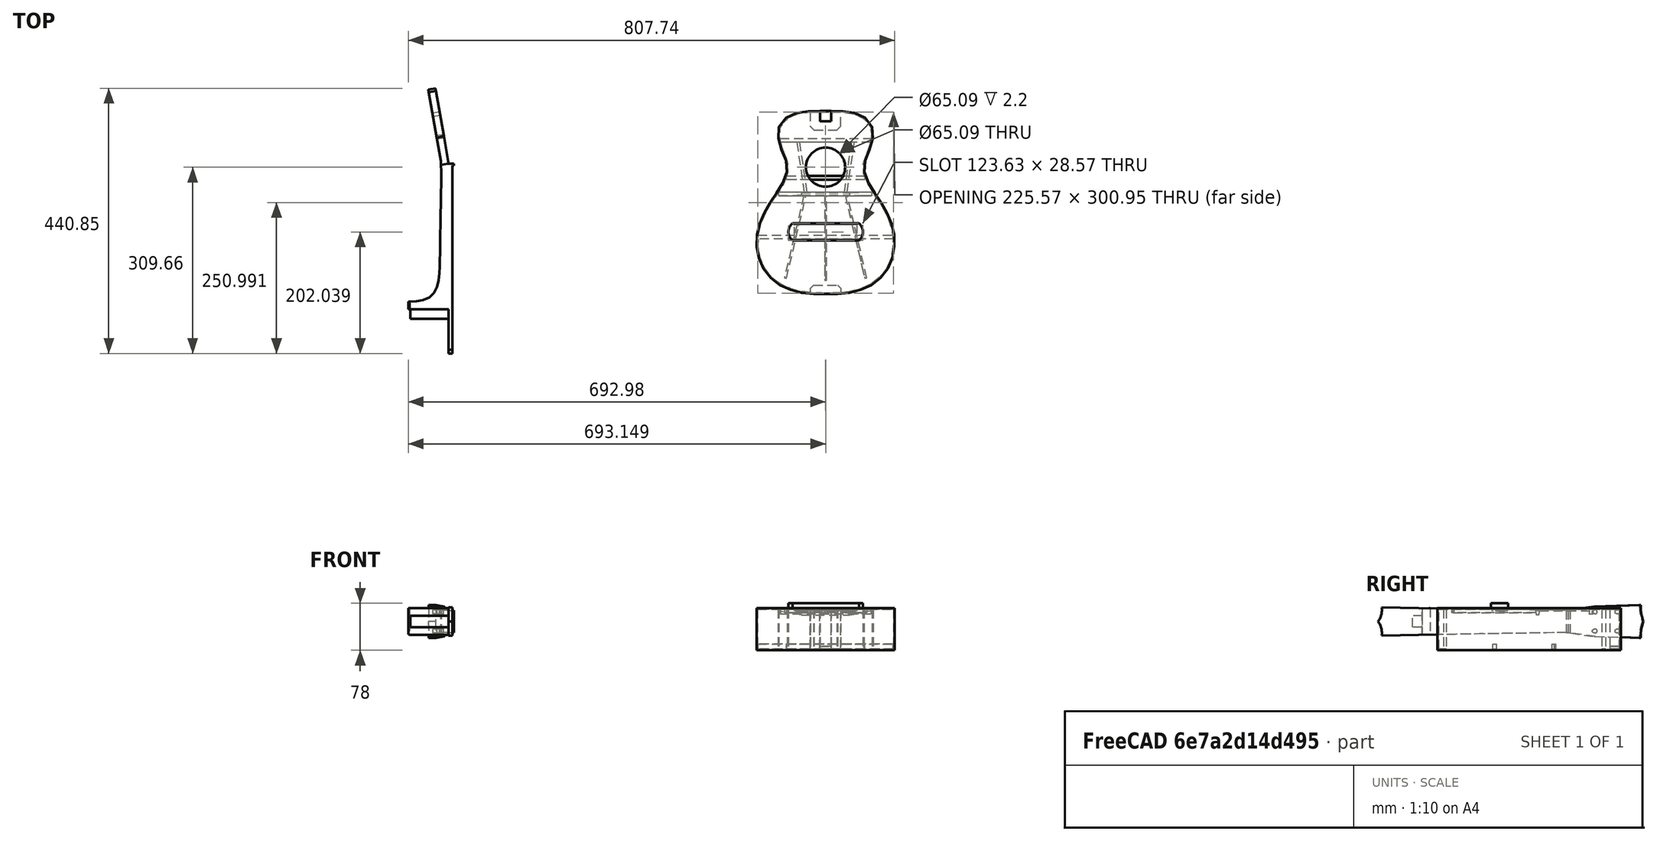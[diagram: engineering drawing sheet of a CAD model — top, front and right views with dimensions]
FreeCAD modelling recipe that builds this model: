
FCSTD DOCUMENT  (FreeCAD 1.0R39109 (Git))
Label: ukulele
License: All rights reserved
LicenseURL: http://en.wikipedia.org/wiki/All_rights_reserved
objects: Sketcher::SketchObject×50, PartDesign::Pad×34, TechDraw::DrawViewDimension×32, PartDesign::Pocket×12, Part::Part2DObjectPython×5, PartDesign::Body×5, TechDraw::DrawProjGroupItem×5, Part::Mirroring×4, App::FeaturePython×4, Spreadsheet::Sheet×3, TechDraw::DrawHatch×3, TechDraw::DrawSVGTemplate×2, App::Part×2, App::Link×2, TechDraw::DrawPage×2, TechDraw::DrawViewDimExtent×2, Image::ImagePlane×1, Part::Feature×1, App::DocumentObjectGroup×1, PartDesign::Hole×1, +3 more types
note: 313 computed .brp shape members not serialized (recipe doc carries the construction recipe); baked Part::Feature solids carry a one-line shape summary decoded from their .brp

FEATURE [Image::ImagePlane] uku
  Placement = pos=(-294.58,-157.27,0) rot=(0,0,1;0rad)
  XSize = 913.808
  YSize = 609.205
FEATURE [Sketcher::SketchObject] Sketch
  ArcFitTolerance = 1e-06
  AttachmentSupport = -> [XY_Plane]
  FullyConstrained = false
  MakeInternals = false
  MapMode = 5
  sketch-geometry (80):
    g0-g17: GeomPoint [constr] x18 (B-spline internal-alignment scaffolding for g18; pole/knot coordinates omitted)
    g18: BSplineCurve PolesCount=20 KnotsCount=18 Degree=3 IsPeriodic=0
    g19-g38: Circle [constr] x20 (B-spline internal-alignment scaffolding for g18; pole/knot coordinates omitted)
    g39: BSplineCurve PolesCount=20 KnotsCount=18 Degree=3 IsPeriodic=0
    g40-g57: GeomPoint [constr] x18 (B-spline internal-alignment scaffolding for g39; pole/knot coordinates omitted)
    g58-g77: Circle [constr] x20 (B-spline internal-alignment scaffolding for g39; pole/knot coordinates omitted)
    g78: LineSegment StartX=-9.55891 StartY=93.6205 StartZ=0 EndX=9.55891 EndY=93.6205 EndZ=0
    g79: LineSegment StartX=-0.843794 StartY=-211.013 StartZ=0 EndX=0.843794 EndY=-211.013 EndZ=0
  constraints (86):
    c: InternalAlignment(g0-g17 -> g18) x18
    c: InternalAlignment(g19,g18)
    c: Weight(g19) = 1
    c: InternalAlignment(g20,g18)
    c: Equal(g20,g19)
    c: InternalAlignment(g21,g18)
    c: Equal(g21,g19)
    c: InternalAlignment(g22,g18)
    c: Equal(g22,g19)
    c: InternalAlignment(g23,g18)
    c: Equal(g23,g19)
    c: InternalAlignment(g24,g18)
    c: Equal(g24,g19)
    c: InternalAlignment(g25,g18)
    c: Equal(g25,g19)
    c: InternalAlignment(g26,g18)
    c: Equal(g26,g19)
    c: InternalAlignment(g27,g18)
    c: Equal(g27,g19)
    c: InternalAlignment(g28,g18)
    c: Equal(g28,g19)
    c: InternalAlignment(g29,g18)
    c: Equal(g29,g19)
    c: InternalAlignment(g30,g18)
    c: Equal(g30,g19)
    c: InternalAlignment(g31,g18)
    c: Equal(g31,g19)
    c: InternalAlignment(g32,g18)
    c: Equal(g32,g19)
    c: InternalAlignment(g33,g18)
    c: Equal(g33,g19)
    c: InternalAlignment(g34,g18)
    c: Equal(g34,g19)
    c: InternalAlignment(g35,g18)
    c: Equal(g35,g19)
    c: InternalAlignment(g36,g18)
    c: Equal(g36,g19)
    c: InternalAlignment(g37,g18)
    c: Equal(g37,g19)
    c: InternalAlignment(g38,g18)
    c: Equal(g38,g19)
    c: InternalAlignment(g40-g77 -> g39) x38
    c: Equal(g19,g58)
    c: Symmetric(g19,g58,g-2)
    c: Equal(g20,g59)
    c: Symmetric(g20,g59,g-2)
    c: Equal(g21,g60)
    c: Symmetric(g21,g60,g-2)
    c: Equal(g22,g61)
    c: Symmetric(g22,g61,g-2)
    c: Equal(g23,g62)
    c: Symmetric(g23,g62,g-2)
    c: Equal(g24,g63)
    c: Symmetric(g24,g63,g-2)
    c: Equal(g25,g64)
    c: Symmetric(g25,g64,g-2)
    c: Equal(g26,g65)
    c: Symmetric(g26,g65,g-2)
    c: Equal(g27,g66)
    c: Symmetric(g27,g66,g-2)
    c: Equal(g28,g67)
    c: Symmetric(g28,g67,g-2)
    c: Equal(g29,g68)
    c: Symmetric(g29,g68,g-2)
    c: Equal(g30,g69)
    c: Symmetric(g30,g69,g-2)
    c: Equal(g31,g70)
    c: Symmetric(g31,g70,g-2)
    c: Equal(g32,g71)
    c: Symmetric(g32,g71,g-2)
    c: Equal(g33,g72)
    c: Symmetric(g33,g72,g-2)
    c: Equal(g34,g73)
    c: Symmetric(g34,g73,g-2)
    c: Equal(g35,g74)
    c: Symmetric(g35,g74,g-2)
    c: Equal(g36,g75)
    c: Symmetric(g36,g75,g-2)
    c: Equal(g37,g76)
    c: Symmetric(g37,g76,g-2)
    c: Equal(g38,g77)
    c: Symmetric(g38,g77,g-2)
    c: Coincident(g78,g18)
    c: Coincident(g78,g39)
    c: Coincident(g79,g18)
    c: Coincident(g79,g39)
FEATURE [Part::Feature] Sketch001
  shape: bbox 230.8 x 304.7 x 2e-07 mm, 0 faces, 0 solids (baked)
FEATURE [Part::Part2DObjectPython] BSpline  # Draft 2D object (typed FeaturePython)
  Area = 0
  Closed = false
  MakeFace = true
  Parameterization = 1
  Points = (23) [(-9.50482,86.1516,0),(-25.8136,85.9069,0),(-41.9527,84.3228,0),(-55.2551,79.961,0),(-66.5807,70.9788,0),(-71.3131,61.8385,0),(-70.9633,44.704,0),+16 more]
FEATURE [PartDesign::Body] Body  label="FIRST_TRY"
  AllowCompound = false
  Group = -> [Sketch,BSpline]
  Origin = -> Origin
FEATURE [Part::Part2DObjectPython] BSpline001  label="outerwall"  # Draft 2D object (typed FeaturePython)
  Area = 0
  Closed = false
  MakeFace = true
  Parameterization = 1
  Points = (31) [(-9.40108,93.5875,0),(-28.0476,93.1013,0),(-45.2362,91.0564,0),(-60.7631,84.8905,0),(-74.8327,72.6147,0),(-79.0928,58.2648,0),(-78.087,44.5074,0),+24 more]
FEATURE [Part::Part2DObjectPython] BSpline002  label="purfling"  # Draft 2D object (typed FeaturePython)
  Area = 0
  Closed = false
  MakeFace = true
  Parameterization = 1
  Points = (31) [(-9.32903,91.8043,0),(-27.9751,91.3181,0),(-44.8193,89.3211,0),(-59.8944,83.3315,0),(-73.3125,71.6798,0),(-77.3133,58.1294,0),(-76.3411,44.8772,0),+24 more]
FEATURE [Part::Part2DObjectPython] BSpline003  label="kerfing"  # Draft 2D object (typed FeaturePython)
  Area = 0
  Closed = false
  MakeFace = true
  Parameterization = 1
  Points = (31) [(-9.11273,86.4502,0),(-27.7574,85.9641,0),(-43.5674,84.1109,0),(-57.2858,78.6508,0),(-68.748,68.8728,0),(-71.9702,57.7226,0),(-71.0989,45.9877,0),+24 more]
FEATURE [Part::Mirroring] Mirror  label="outerwall (mirrored)"
  Base = (0,0,0)
  Normal = (1,0,0)
  Source = -> BSpline001
FEATURE [Part::Mirroring] Mirror001  label="kerfing (mirrored)"
  Base = (0,0,0)
  Normal = (1,0,0)
  Source = -> BSpline003
FEATURE [Part::Mirroring] Mirror002  label="purfling (mirrored)"
  Base = (0,0,0)
  Normal = (1,0,0)
  Source = -> BSpline002
FEATURE [Sketcher::SketchObject] Sketch002  label="base sketch"
  ArcFitTolerance = 1e-06
  FullyConstrained = false
  MakeInternals = false
  sketch-geometry (198):
    g0: BSplineCurve PolesCount=33 KnotsCount=31 Degree=3 IsPeriodic=0
    g1-g33: Circle [constr] x33 (B-spline internal-alignment scaffolding for g0; pole/knot coordinates omitted)
    g34-g64: GeomPoint [constr] x31 (B-spline internal-alignment scaffolding for g0; pole/knot coordinates omitted)
    g65: BSplineCurve PolesCount=33 KnotsCount=31 Degree=3 IsPeriodic=0
    g66-g98: Circle [constr] x33 (B-spline internal-alignment scaffolding for g65; pole/knot coordinates omitted)
    g99-g129: GeomPoint [constr] x31 (B-spline internal-alignment scaffolding for g65; pole/knot coordinates omitted)
    g130: BSplineCurve PolesCount=33 KnotsCount=31 Degree=3 IsPeriodic=0
    g131-g163: Circle [constr] x33 (B-spline internal-alignment scaffolding for g130; pole/knot coordinates omitted)
    g164-g194: GeomPoint [constr] x31 (B-spline internal-alignment scaffolding for g130; pole/knot coordinates omitted)
    g195: BSplineCurve PolesCount=33 KnotsCount=31 Degree=3 IsPeriodic=0
    g196: BSplineCurve PolesCount=33 KnotsCount=31 Degree=3 IsPeriodic=0
    g197: BSplineCurve PolesCount=33 KnotsCount=31 Degree=3 IsPeriodic=0
  constraints (201):
    c: InternalAlignment(g1,g0)
    c: Weight(g1) = 1
    c: InternalAlignment(g2,g0)
    c: Equal(g2,g1)
    c: InternalAlignment(g3,g0)
    c: Equal(g3,g1)
    c: InternalAlignment(g4,g0)
    c: Equal(g4,g1)
    c: InternalAlignment(g5,g0)
    c: Equal(g5,g1)
    c: InternalAlignment(g6,g0)
    c: Equal(g6,g1)
    c: InternalAlignment(g7,g0)
    c: Equal(g7,g1)
    c: InternalAlignment(g8,g0)
    c: Equal(g8,g1)
    c: InternalAlignment(g9,g0)
    c: Equal(g9,g1)
    c: InternalAlignment(g10,g0)
    c: Equal(g10,g1)
    c: InternalAlignment(g11,g0)
    c: Equal(g11,g1)
    c: InternalAlignment(g12,g0)
    c: Equal(g12,g1)
    c: InternalAlignment(g13,g0)
    c: Equal(g13,g1)
    c: InternalAlignment(g14,g0)
    c: Equal(g14,g1)
    c: InternalAlignment(g15,g0)
    c: Equal(g15,g1)
    c: InternalAlignment(g16,g0)
    c: Equal(g16,g1)
    c: InternalAlignment(g17,g0)
    c: Equal(g17,g1)
    c: InternalAlignment(g18,g0)
    c: Equal(g18,g1)
    c: InternalAlignment(g19,g0)
    c: Equal(g19,g1)
    c: InternalAlignment(g20,g0)
    c: Equal(g20,g1)
    c: InternalAlignment(g21,g0)
    c: Equal(g21,g1)
    c: InternalAlignment(g22,g0)
    c: Equal(g22,g1)
    c: InternalAlignment(g23,g0)
    c: Equal(g23,g1)
    c: InternalAlignment(g24,g0)
    c: Equal(g24,g1)
    c: InternalAlignment(g25,g0)
    c: Equal(g25,g1)
    c: InternalAlignment(g26,g0)
    c: Equal(g26,g1)
    c: InternalAlignment(g27,g0)
    c: Equal(g27,g1)
    c: InternalAlignment(g28,g0)
    c: Equal(g28,g1)
    c: InternalAlignment(g29,g0)
    c: Equal(g29,g1)
    c: InternalAlignment(g30,g0)
    c: Equal(g30,g1)
    c: InternalAlignment(g31,g0)
    c: Equal(g31,g1)
    c: InternalAlignment(g32,g0)
    c: Equal(g32,g1)
    c: InternalAlignment(g33,g0)
    c: Equal(g33,g1)
    c: InternalAlignment(g34-g64 -> g0) x31
    c: InternalAlignment(g66,g65)
    c: Weight(g66) = 1
    c: InternalAlignment(g67,g65)
    c: Equal(g67,g66)
    c: InternalAlignment(g68,g65)
    c: Equal(g68,g66)
    c: InternalAlignment(g69,g65)
    c: Equal(g69,g66)
    c: InternalAlignment(g70,g65)
    c: Equal(g70,g66)
    c: InternalAlignment(g71,g65)
    c: Equal(g71,g66)
    c: InternalAlignment(g72,g65)
    c: Equal(g72,g66)
    c: InternalAlignment(g73,g65)
    c: Equal(g73,g66)
    c: InternalAlignment(g74,g65)
    c: Equal(g74,g66)
    c: InternalAlignment(g75,g65)
    c: Equal(g75,g66)
    c: InternalAlignment(g76,g65)
    c: Equal(g76,g66)
    c: InternalAlignment(g77,g65)
    c: Equal(g77,g66)
    c: InternalAlignment(g78,g65)
    c: Equal(g78,g66)
    c: InternalAlignment(g79,g65)
    c: Equal(g79,g66)
    c: InternalAlignment(g80,g65)
    c: Equal(g80,g66)
    c: InternalAlignment(g81,g65)
    c: Equal(g81,g66)
    c: InternalAlignment(g82,g65)
    c: Equal(g82,g66)
    c: InternalAlignment(g83,g65)
    c: Equal(g83,g66)
    c: InternalAlignment(g84,g65)
    c: Equal(g84,g66)
    c: InternalAlignment(g85,g65)
    c: Equal(g85,g66)
    c: InternalAlignment(g86,g65)
    c: Equal(g86,g66)
    c: InternalAlignment(g87,g65)
    c: Equal(g87,g66)
    c: InternalAlignment(g88,g65)
    c: Equal(g88,g66)
    c: InternalAlignment(g89,g65)
    c: Equal(g89,g66)
    c: InternalAlignment(g90,g65)
    c: Equal(g90,g66)
    c: InternalAlignment(g91,g65)
    c: Equal(g91,g66)
    c: InternalAlignment(g92,g65)
    c: Equal(g92,g66)
    c: InternalAlignment(g93,g65)
    c: Equal(g93,g66)
    c: InternalAlignment(g94,g65)
    c: Equal(g94,g66)
    c: InternalAlignment(g95,g65)
    c: Equal(g95,g66)
    c: InternalAlignment(g96,g65)
    c: Equal(g96,g66)
    c: InternalAlignment(g97,g65)
    c: Equal(g97,g66)
    c: InternalAlignment(g98,g65)
    c: Equal(g98,g66)
    c: InternalAlignment(g99-g129 -> g65) x31
    c: InternalAlignment(g131,g130)
    c: Weight(g131) = 1
    c: InternalAlignment(g132,g130)
    c: Equal(g132,g131)
    c: InternalAlignment(g133,g130)
    c: Equal(g133,g131)
    c: InternalAlignment(g134,g130)
    c: Equal(g134,g131)
    c: InternalAlignment(g135,g130)
    c: Equal(g135,g131)
    c: InternalAlignment(g136,g130)
    c: Equal(g136,g131)
    c: InternalAlignment(g137,g130)
    c: Equal(g137,g131)
    c: InternalAlignment(g138,g130)
    c: Equal(g138,g131)
    c: InternalAlignment(g139,g130)
    c: Equal(g139,g131)
    c: InternalAlignment(g140,g130)
    c: Equal(g140,g131)
    c: InternalAlignment(g141,g130)
    c: Equal(g141,g131)
    c: InternalAlignment(g142,g130)
    c: Equal(g142,g131)
    c: InternalAlignment(g143,g130)
    c: Equal(g143,g131)
    c: InternalAlignment(g144,g130)
    c: Equal(g144,g131)
    c: InternalAlignment(g145,g130)
    c: Equal(g145,g131)
    c: InternalAlignment(g146,g130)
    c: Equal(g146,g131)
    c: InternalAlignment(g147,g130)
    c: Equal(g147,g131)
    c: InternalAlignment(g148,g130)
    c: Equal(g148,g131)
    c: InternalAlignment(g149,g130)
    c: Equal(g149,g131)
    c: InternalAlignment(g150,g130)
    c: Equal(g150,g131)
    c: InternalAlignment(g151,g130)
    c: Equal(g151,g131)
    c: InternalAlignment(g152,g130)
    c: Equal(g152,g131)
    c: InternalAlignment(g153,g130)
    c: Equal(g153,g131)
    c: InternalAlignment(g154,g130)
    c: Equal(g154,g131)
    c: InternalAlignment(g155,g130)
    c: Equal(g155,g131)
    c: InternalAlignment(g156,g130)
    c: Equal(g156,g131)
    c: InternalAlignment(g157,g130)
    c: Equal(g157,g131)
    c: InternalAlignment(g158,g130)
    c: Equal(g158,g131)
    c: InternalAlignment(g159,g130)
    c: Equal(g159,g131)
    c: InternalAlignment(g160,g130)
    c: Equal(g160,g131)
    c: InternalAlignment(g161,g130)
    c: Equal(g161,g131)
    c: InternalAlignment(g162,g130)
    c: Equal(g162,g131)
    c: InternalAlignment(g163,g130)
    c: Equal(g163,g131)
    c: InternalAlignment(g164-g194 -> g130) x31
FEATURE [Sketcher::SketchObject] Sketch003  label="vk"
  ArcFitTolerance = 1e-06
  FullyConstrained = false
  MakeInternals = false
  sketch-geometry (68):
    g0: BSplineCurve PolesCount=33 KnotsCount=31 Degree=3 IsPeriodic=0
    g1-g33: Circle [constr] x33 (B-spline internal-alignment scaffolding for g0; pole/knot coordinates omitted)
    g34-g64: GeomPoint [constr] x31 (B-spline internal-alignment scaffolding for g0; pole/knot coordinates omitted)
    g65: BSplineCurve PolesCount=33 KnotsCount=31 Degree=3 IsPeriodic=0
    g66: LineSegment StartX=-9.40108 StartY=93.5875 StartZ=0 EndX=9.40107 EndY=93.5875 EndZ=0
    g67: LineSegment StartX=-0.637124 StartY=-210.927 StartZ=0 EndX=0.637124 EndY=-210.927 EndZ=0
  constraints (73):
    c: InternalAlignment(g1,g0)
    c: Weight(g1) = 1
    c: InternalAlignment(g2,g0)
    c: Equal(g2,g1)
    c: InternalAlignment(g3,g0)
    c: Equal(g3,g1)
    c: InternalAlignment(g4,g0)
    c: Equal(g4,g1)
    c: InternalAlignment(g5,g0)
    c: Equal(g5,g1)
    c: InternalAlignment(g6,g0)
    c: Equal(g6,g1)
    c: InternalAlignment(g7,g0)
    c: Equal(g7,g1)
    c: InternalAlignment(g8,g0)
    c: Equal(g8,g1)
    c: InternalAlignment(g9,g0)
    c: Equal(g9,g1)
    c: InternalAlignment(g10,g0)
    c: Equal(g10,g1)
    c: InternalAlignment(g11,g0)
    c: Equal(g11,g1)
    c: InternalAlignment(g12,g0)
    c: Equal(g12,g1)
    c: InternalAlignment(g13,g0)
    c: Equal(g13,g1)
    c: InternalAlignment(g14,g0)
    c: Equal(g14,g1)
    c: InternalAlignment(g15,g0)
    c: Equal(g15,g1)
    c: InternalAlignment(g16,g0)
    c: Equal(g16,g1)
    c: InternalAlignment(g17,g0)
    c: Equal(g17,g1)
    c: InternalAlignment(g18,g0)
    c: Equal(g18,g1)
    c: InternalAlignment(g19,g0)
    c: Equal(g19,g1)
    c: InternalAlignment(g20,g0)
    c: Equal(g20,g1)
    c: InternalAlignment(g21,g0)
    c: Equal(g21,g1)
    c: InternalAlignment(g22,g0)
    c: Equal(g22,g1)
    c: InternalAlignment(g23,g0)
    c: Equal(g23,g1)
    c: InternalAlignment(g24,g0)
    c: Equal(g24,g1)
    c: InternalAlignment(g25,g0)
    c: Equal(g25,g1)
    c: InternalAlignment(g26,g0)
    c: Equal(g26,g1)
    c: InternalAlignment(g27,g0)
    c: Equal(g27,g1)
    c: InternalAlignment(g28,g0)
    c: Equal(g28,g1)
    c: InternalAlignment(g29,g0)
    c: Equal(g29,g1)
    c: InternalAlignment(g30,g0)
    c: Equal(g30,g1)
    c: InternalAlignment(g31,g0)
    c: Equal(g31,g1)
    c: InternalAlignment(g32,g0)
    c: Equal(g32,g1)
    c: InternalAlignment(g33,g0)
    c: Equal(g33,g1)
    c: InternalAlignment(g34-g64 -> g0) x31
    c: Coincident(g66,g0)
    c: Coincident(g66,g65)
    c: Horizontal(g66)
    c: Coincident(g67,g0)
    c: Coincident(g67,g65)
    c: Horizontal(g67)
FEATURE [PartDesign::Pad] Pad
  Direction = (0,0,1)
  Length = 2.2
  Length2 = 10
  Profile = -> Sketch003
  ReferenceAxis = -> Sketch003 [N_Axis]
  Reversed = true
  Suppressed = false
  Type = 0
  expr: Length = <<dimensies>>.DIKTE_FRONT
FEATURE [Spreadsheet::Sheet] Spreadsheet  label="dimensies"
  cells = A3='dikte front; B3(DIKTE_FRONT)=2.2; C3='mm; A4='diepte; B4(DIEPTE)=70
FEATURE [Sketcher::SketchObject] Sketch004
  ArcFitTolerance = 1e-06
  AttachmentSupport = -> [XY_Plane001]
  FullyConstrained = true
  MakeInternals = false
  MapMode = 5
  sketch-geometry (1):
    g0: Circle CenterX=0 CenterY=0 CenterZ=0 NormalX=0 NormalY=0 NormalZ=1 AngleXU=0 Radius=32.5435
  constraints (2):
    c: Coincident(g0,g-1)
    c: Diameter(g0) = 65.087
FEATURE [PartDesign::Pocket] Pocket
  BaseFeature = -> Pad
  Direction = (0,0,-1)
  Length = 5
  Length2 = 5
  Profile = -> Sketch004
  ReferenceAxis = -> Sketch004 [N_Axis]
  Suppressed = false
  Type = 2
FEATURE [Part::Part2DObjectPython] BSpline005  label="innerwall"  # Draft 2D object (typed FeaturePython)
  Area = 0
  Closed = false
  MakeFace = true
  Parameterization = 1
  Points = (31) [(-9.3204,91.5907,0),(-27.9664,91.1045,0),(-44.7693,89.1132,0),(-59.7903,83.1448,0),(-73.1303,71.5678,0),(-77.1001,58.1131,0),(-76.132,44.9215,0),+24 more]
FEATURE [Part::Mirroring] Mirror003  label="innerwall (mirrored)"
  Base = (0,-58.6691,0)
  Normal = (1,0,-1.19209e-07)
  Source = -> BSpline005
FEATURE [App::DocumentObjectGroup] Group  label="drafting"
  Group = -> [BSpline001,BSpline003,BSpline002,Mirror,Mirror002,Mirror001,BSpline005,Mirror003]
FEATURE [Sketcher::SketchObject] Sketch005  label="base sketch001"
  ArcFitTolerance = 1e-06
  FullyConstrained = false
  MakeInternals = false
  sketch-geometry (136):
    g0: BSplineCurve PolesCount=33 KnotsCount=31 Degree=3 IsPeriodic=0
    g1-g33: Circle [constr] x33 (B-spline internal-alignment scaffolding for g0; pole/knot coordinates omitted)
    g34-g64: GeomPoint [constr] x31 (B-spline internal-alignment scaffolding for g0; pole/knot coordinates omitted)
    g65: BSplineCurve PolesCount=33 KnotsCount=31 Degree=3 IsPeriodic=0
    g66-g98: Circle [constr] x33 (B-spline internal-alignment scaffolding for g65; pole/knot coordinates omitted)
    g99-g129: GeomPoint [constr] x31 (B-spline internal-alignment scaffolding for g65; pole/knot coordinates omitted)
    g130: BSplineCurve PolesCount=33 KnotsCount=31 Degree=3 IsPeriodic=0
    g131: BSplineCurve PolesCount=33 KnotsCount=31 Degree=3 IsPeriodic=0
    g132: LineSegment StartX=-9.32903 StartY=91.8043 StartZ=0 EndX=9.32903 EndY=91.8043 EndZ=0
    g133: LineSegment StartX=-9.40108 StartY=93.5875 StartZ=0 EndX=9.40107 EndY=93.5875 EndZ=0
    g134: LineSegment StartX=-0.629425 StartY=-209.143 StartZ=0 EndX=0.629425 EndY=-209.143 EndZ=0
    g135: LineSegment StartX=-0.637124 StartY=-210.927 StartZ=0 EndX=0.637124 EndY=-210.927 EndZ=0
  constraints (146):
    c: InternalAlignment(g1,g0)
    c: Weight(g1) = 1
    c: InternalAlignment(g2,g0)
    c: Equal(g2,g1)
    c: InternalAlignment(g3,g0)
    c: Equal(g3,g1)
    c: InternalAlignment(g4,g0)
    c: Equal(g4,g1)
    c: InternalAlignment(g5,g0)
    c: Equal(g5,g1)
    c: InternalAlignment(g6,g0)
    c: Equal(g6,g1)
    c: InternalAlignment(g7,g0)
    c: Equal(g7,g1)
    c: InternalAlignment(g8,g0)
    c: Equal(g8,g1)
    c: InternalAlignment(g9,g0)
    c: Equal(g9,g1)
    c: InternalAlignment(g10,g0)
    c: Equal(g10,g1)
    c: InternalAlignment(g11,g0)
    c: Equal(g11,g1)
    c: InternalAlignment(g12,g0)
    c: Equal(g12,g1)
    c: InternalAlignment(g13,g0)
    c: Equal(g13,g1)
    c: InternalAlignment(g14,g0)
    c: Equal(g14,g1)
    c: InternalAlignment(g15,g0)
    c: Equal(g15,g1)
    c: InternalAlignment(g16,g0)
    c: Equal(g16,g1)
    c: InternalAlignment(g17,g0)
    c: Equal(g17,g1)
    c: InternalAlignment(g18,g0)
    c: Equal(g18,g1)
    c: InternalAlignment(g19,g0)
    c: Equal(g19,g1)
    c: InternalAlignment(g20,g0)
    c: Equal(g20,g1)
    c: InternalAlignment(g21,g0)
    c: Equal(g21,g1)
    c: InternalAlignment(g22,g0)
    c: Equal(g22,g1)
    c: InternalAlignment(g23,g0)
    c: Equal(g23,g1)
    c: InternalAlignment(g24,g0)
    c: Equal(g24,g1)
    c: InternalAlignment(g25,g0)
    c: Equal(g25,g1)
    c: InternalAlignment(g26,g0)
    c: Equal(g26,g1)
    c: InternalAlignment(g27,g0)
    c: Equal(g27,g1)
    c: InternalAlignment(g28,g0)
    c: Equal(g28,g1)
    c: InternalAlignment(g29,g0)
    c: Equal(g29,g1)
    c: InternalAlignment(g30,g0)
    c: Equal(g30,g1)
    c: InternalAlignment(g31,g0)
    c: Equal(g31,g1)
    c: InternalAlignment(g32,g0)
    c: Equal(g32,g1)
    c: InternalAlignment(g33,g0)
    c: Equal(g33,g1)
    c: InternalAlignment(g34-g64 -> g0) x31
    c: InternalAlignment(g66,g65)
    c: Weight(g66) = 1
    c: InternalAlignment(g67,g65)
    c: Equal(g67,g66)
    c: InternalAlignment(g68,g65)
    c: Equal(g68,g66)
    c: InternalAlignment(g69,g65)
    c: Equal(g69,g66)
    c: InternalAlignment(g70,g65)
    c: Equal(g70,g66)
    c: InternalAlignment(g71,g65)
    c: Equal(g71,g66)
    c: InternalAlignment(g72,g65)
    c: Equal(g72,g66)
    c: InternalAlignment(g73,g65)
    c: Equal(g73,g66)
    c: InternalAlignment(g74,g65)
    c: Equal(g74,g66)
    c: InternalAlignment(g75,g65)
    c: Equal(g75,g66)
    c: InternalAlignment(g76,g65)
    c: Equal(g76,g66)
    c: InternalAlignment(g77,g65)
    c: Equal(g77,g66)
    c: InternalAlignment(g78,g65)
    c: Equal(g78,g66)
    c: InternalAlignment(g79,g65)
    c: Equal(g79,g66)
    c: InternalAlignment(g80,g65)
    c: Equal(g80,g66)
    c: InternalAlignment(g81,g65)
    c: Equal(g81,g66)
    c: InternalAlignment(g82,g65)
    c: Equal(g82,g66)
    c: InternalAlignment(g83,g65)
    c: Equal(g83,g66)
    c: InternalAlignment(g84,g65)
    c: Equal(g84,g66)
    c: InternalAlignment(g85,g65)
    c: Equal(g85,g66)
    c: InternalAlignment(g86,g65)
    c: Equal(g86,g66)
    c: InternalAlignment(g87,g65)
    c: Equal(g87,g66)
    c: InternalAlignment(g88,g65)
    c: Equal(g88,g66)
    c: InternalAlignment(g89,g65)
    c: Equal(g89,g66)
    c: InternalAlignment(g90,g65)
    c: Equal(g90,g66)
    c: InternalAlignment(g91,g65)
    c: Equal(g91,g66)
    c: InternalAlignment(g92,g65)
    c: Equal(g92,g66)
    c: InternalAlignment(g93,g65)
    c: Equal(g93,g66)
    c: InternalAlignment(g94,g65)
    c: Equal(g94,g66)
    c: InternalAlignment(g95,g65)
    c: Equal(g95,g66)
    c: InternalAlignment(g96,g65)
    c: Equal(g96,g66)
    c: InternalAlignment(g97,g65)
    c: Equal(g97,g66)
    c: InternalAlignment(g98,g65)
    c: Equal(g98,g66)
    c: InternalAlignment(g99-g129 -> g65) x31
    c: Coincident(g132,g65)
    c: Coincident(g132,g131)
    c: Horizontal(g132)
    c: Coincident(g133,g0)
    c: Coincident(g133,g130)
    c: Horizontal(g133)
    c: Coincident(g134,g65)
    c: Coincident(g134,g131)
    c: Horizontal(g134)
    c: Coincident(g135,g0)
    c: Coincident(g135,g130)
    c: Horizontal(g135)
FEATURE [PartDesign::Pad] Pad001
  BaseFeature = -> Pocket
  Direction = (0,0,1)
  Length = 70
  Length2 = 10
  Profile = -> Sketch005
  ReferenceAxis = -> Sketch005 [N_Axis]
  Refine = true
  Reversed = true
  Suppressed = false
  Type = 0
  expr: Length = 70
FEATURE [Sketcher::SketchObject] Sketch006
  ArcFitTolerance = 1e-06
  AttachmentSupport = -> [YZ_Plane001]
  ExternalGeometry = -> [Pad001]
  FullyConstrained = true
  MakeInternals = false
  MapMode = 5
  Placement = pos=(0,0,0) rot=(0.57735,0.57735,0.57735;2.0944rad)
  sketch-geometry (10):
    g0: GeomPoint X=0 Y=-2.2 Z=0
    g1: GeomPoint X=-44.45 Y=-2.2 Z=0
    g2: GeomPoint X=44.45 Y=-2.2 Z=0
    g3: LineSegment StartX=-47.625 StartY=-2.2 StartZ=0 EndX=-41.275 EndY=-2.2 EndZ=0
    g4: LineSegment StartX=-41.275 StartY=-2.2 StartZ=0 EndX=-41.275 EndY=-7.2 EndZ=0
    g5: LineSegment StartX=-41.275 StartY=-7.2 StartZ=0 EndX=-42.45 EndY=-11.725 EndZ=0
    g6: LineSegment StartX=-42.45 StartY=-11.725 StartZ=0 EndX=-46.45 EndY=-11.725 EndZ=0
    g7: LineSegment StartX=-46.45 StartY=-11.725 StartZ=0 EndX=-47.625 EndY=-7.2 EndZ=0
    g8: LineSegment StartX=-47.625 StartY=-7.2 StartZ=0 EndX=-47.625 EndY=-2.2 EndZ=0
    g9: GeomPoint X=-44.45 Y=-11.725 Z=0
  constraints (24):
    c: PointOnObject(g0,g-4)
    c: PointOnObject(g1,g-4)
    c: DistanceX(g1,g0) = 44.45
    c: Symmetric(g1,g2,g0)
    c: PointOnObject(g0,g-2)
    c: PointOnObject(g3,g-4)
    c: PointOnObject(g3,g-4)
    c: Coincident(g3,g4)
    c: Vertical(g4)
    c: Coincident(g4,g5)
    c: Coincident(g5,g6)
    c: Horizontal(g6)
    c: Coincident(g6,g7)
    c: Coincident(g7,g8)
    c: Coincident(g8,g3)
    c: Symmetric(g3,g3,g1)
    c: Vertical(g8)
    c: DistanceX(g3,g3) = 6.35
    c: Horizontal(g4,g7)
    c: DistanceY(g5,g3) = 9.525
    c: DistanceY(g8,g8) = 5
    c: Symmetric(g6,g6,g9)
    c: Vertical(g9,g1)
    c: DistanceX(g6,g9) = 2
FEATURE [PartDesign::Pad] Pad002
  BaseFeature = -> Pad001
  Direction = (1,0,0)
  Length = 155
  Length2 = 10
  Midplane = true
  Profile = -> Sketch006
  ReferenceAxis = -> Sketch006 [N_Axis]
  Refine = true
  Suppressed = false
  Type = 0
FEATURE [Sketcher::SketchObject] Sketch007
  ArcFitTolerance = 1e-06
  AttachmentSupport = -> [Pad002]
  ExternalGeometry = -> [Pad002]
  FullyConstrained = true
  MakeInternals = false
  MapMode = 5
  Placement = pos=(0,-41.275,0) rot=(0,0.707107,0.707107;3.14159rad)
  sketch-geometry (12):
    g0: GeomPoint X=40 Y=-11.725 Z=0
    g1: GeomPoint X=-40 Y=-11.725 Z=0
    g2: GeomPoint X=0 Y=-7.2 Z=0
    g3: GeomPoint X=-78.3882 Y=-4.2 Z=0
    g4: GeomPoint X=78.3882 Y=-4.2 Z=0
    g5: LineSegment StartX=78.3882 StartY=-4.2 StartZ=0 EndX=40 EndY=-11.725 EndZ=0
    g6: LineSegment StartX=-40 StartY=-11.725 StartZ=0 EndX=-78.3882 EndY=-4.2 EndZ=0
    g7: LineSegment StartX=40 StartY=-11.725 StartZ=0 EndX=-40 EndY=-11.725 EndZ=0
    g8: LineSegment StartX=78.3882 StartY=-4.2 StartZ=0 EndX=78.3882 EndY=-24.2 EndZ=0
    g9: LineSegment StartX=78.3882 StartY=-24.2 StartZ=0 EndX=-78.3882 EndY=-24.2 EndZ=0
    g10: LineSegment StartX=-78.3882 StartY=-4.2 StartZ=0 EndX=-78.3882 EndY=-24.2 EndZ=0
    g11: GeomPoint X=0 Y=-11.725 Z=0
  constraints (24):
    c: Symmetric(g-4,g-4,g2)
    c: PointOnObject(g3,g-6)
    c: PointOnObject(g4,g-5)
    c: Horizontal(g4,g3)
    c: DistanceX(g2,g0) = 40
    c: Coincident(g5,g4)
    c: Coincident(g5,g0)
    c: Coincident(g6,g1)
    c: DistanceY(g4,g-5) = 2
    c: Coincident(g7,g0)
    c: Coincident(g7,g1)
    c: Coincident(g8,g4)
    c: Vertical(g8)
    c: Coincident(g9,g8)
    c: Horizontal(g9)
    c: Coincident(g10,g9)
    c: Vertical(g10)
    c: DistanceY(g10,g10) = 20
    c: Coincident(g3,g10)
    c: Coincident(g3,g6)
    c: PointOnObject(g11,g-7)
    c: PointOnObject(g11,g-2)
    c: Symmetric(g1,g0,g11)
    c: Horizontal(g7)
FEATURE [PartDesign::Pocket] Pocket001
  BaseFeature = -> Pad002
  Direction = (0,-1,2e-16)
  Length = 9
  Length2 = 5
  Profile = -> Sketch007
  ReferenceAxis = -> Sketch007 [N_Axis]
  Refine = true
  Suppressed = false
  Type = 0
FEATURE [Sketcher::SketchObject] Sketch008
  ArcFitTolerance = 1e-06
  AttachmentSupport = -> [Pocket001]
  ExternalGeometry = -> [Pocket001]
  FullyConstrained = true
  MakeInternals = false
  MapMode = 5
  Placement = pos=(0,0,-2.2) rot=(1,0,0;3.14159rad)
  sketch-geometry (8):
    g0: LineSegment StartX=-25 StartY=209.143 StartZ=0 EndX=25 EndY=209.143 EndZ=0
    g1: GeomPoint X=-2.2048e-07 Y=209.143 Z=0
    g2: LineSegment StartX=-25 StartY=209.143 StartZ=0 EndX=-25 EndY=201.143 EndZ=0
    g3: LineSegment StartX=-25 StartY=201.143 StartZ=0 EndX=-20 EndY=196.143 EndZ=0
    g4: LineSegment StartX=-20 StartY=196.143 StartZ=0 EndX=20 EndY=196.143 EndZ=0
    g5: LineSegment StartX=20 StartY=196.143 StartZ=0 EndX=25 EndY=201.143 EndZ=0
    g6: LineSegment StartX=25 StartY=201.143 StartZ=0 EndX=25 EndY=209.143 EndZ=0
    g7: GeomPoint X=0 Y=196.143 Z=0
  constraints (19):
    c: Horizontal(g0)
    c: Symmetric(g0,g0,g1)
    c: Symmetric(g-4,g-3,g1)
    c: DistanceX(g0,g0) = 50
    c: Coincident(g0,g2)
    c: Vertical(g2)
    c: Coincident(g2,g3)
    c: Coincident(g3,g4)
    c: Horizontal(g4)
    c: Coincident(g4,g5)
    c: Coincident(g5,g6)
    c: Coincident(g6,g0)
    c: Vertical(g6)
    c: Symmetric(g4,g4,g7)
    c: PointOnObject(g7,g-2)
    c: Angle(g3,g2) = 2.35619
    c: DistanceY(g6,g6) = 8
    c: DistanceX(g4,g4) = 40
    c: Horizontal(g2,g5)
FEATURE [PartDesign::Pad] Pad003
  BaseFeature = -> Pocket001
  Direction = (0,0,-1)
  Length = 65.6
  Length2 = 10
  Profile = -> Sketch008
  ReferenceAxis = -> Sketch008 [N_Axis]
  Refine = true
  Suppressed = false
  Type = 0
  expr: Length = <<dimensies>>.DIEPTE - 2 * <<dimensies>>.DIKTE_FRONT
FEATURE [Sketcher::SketchObject] Sketch009
  ArcFitTolerance = 1e-06
  AttachmentSupport = -> [Pad003]
  FullyConstrained = true
  MakeInternals = false
  MapMode = 5
  Placement = pos=(0,0,-2.2) rot=(1,0,0;3.14159rad)
  sketch-geometry (12):
    g0: LineSegment StartX=-25.4 StartY=-92.925 StartZ=0 EndX=-25.4 EndY=-68.289 EndZ=0
    g1: LineSegment StartX=-25.4 StartY=-68.289 StartZ=0 EndX=-19.036 EndY=-61.925 EndZ=0
    g2: LineSegment StartX=-19.036 StartY=-61.925 StartZ=0 EndX=19.036 EndY=-61.925 EndZ=0
    g3: LineSegment StartX=19.036 StartY=-61.925 StartZ=0 EndX=25.4 EndY=-68.289 EndZ=0
    g4: LineSegment StartX=25.4 StartY=-68.289 StartZ=0 EndX=25.4 EndY=-92.925 EndZ=0
    g5: LineSegment StartX=25.4 StartY=-92.925 StartZ=0 EndX=9.525 EndY=-92.925 EndZ=0
    g6: LineSegment StartX=9.525 StartY=-92.925 StartZ=0 EndX=9.525 EndY=-75.525 EndZ=0
    g7: LineSegment StartX=9.525 StartY=-75.525 StartZ=0 EndX=-9.525 EndY=-75.525 EndZ=0
    g8: LineSegment StartX=-9.525 StartY=-75.525 StartZ=0 EndX=-9.525 EndY=-92.925 EndZ=0
    g9: LineSegment StartX=-9.525 StartY=-92.925 StartZ=0 EndX=-25.4 EndY=-92.925 EndZ=0
    g10: GeomPoint X=0 Y=-61.925 Z=0
    g11: GeomPoint X=0 Y=-75.525 Z=0
  constraints (32):
    c: Vertical(g0)
    c: Coincident(g0,g1)
    c: Coincident(g1,g2)
    c: Horizontal(g2)
    c: Coincident(g2,g3)
    c: Coincident(g3,g4)
    c: Vertical(g4)
    c: Coincident(g4,g5)
    c: Horizontal(g5)
    c: Coincident(g5,g6)
    c: Vertical(g6)
    c: Coincident(g6,g7)
    c: Horizontal(g7)
    c: Coincident(g7,g8)
    c: Vertical(g8)
    c: Coincident(g8,g9)
    c: Coincident(g9,g0)
    c: Horizontal(g9)
    c: Symmetric(g2,g2,g10)
    c: Symmetric(g7,g7,g11)
    c: PointOnObject(g11,g-2)
    c: PointOnObject(g10,g-2)
    c: Angle(g0,g1) = 2.35619
    c: Horizontal(g3,g0)
    c: Equal(g9,g5)
    c: DistanceX(g8,g5) = 19.05
    c: DistanceY(g0,g1) = 31
    c: DistanceY(g8,g8) = 17.4
    c: Horizontal(g8,g5)
    c: DistanceX(g0,g4) = 50.8
    c: Distance(g1,g1) = 9
    c: Block(g2)
FEATURE [PartDesign::Pad] Pad004
  BaseFeature = -> Pad003
  Direction = (0,0,-1)
  Length = 65.6
  Length2 = 10
  Profile = -> Sketch009
  ReferenceAxis = -> Sketch009 [N_Axis]
  Refine = true
  Suppressed = false
  Type = 0
  expr: Length = <<dimensies>>.DIEPTE - 2 * <<dimensies>>.DIKTE_FRONT
FEATURE [Sketcher::SketchObject] Sketch010
  ArcFitTolerance = 1e-06
  AttachmentSupport = -> [Pad004]
  ExternalGeometry = -> [Pad004,Sketch003]
  FullyConstrained = true
  MakeInternals = false
  MapMode = 5
  Placement = pos=(0,93.5875,0) rot=(0,0.707107,0.707107;3.14159rad)
  sketch-geometry (4):
    g0: LineSegment StartX=-9.40107 StartY=0 StartZ=0 EndX=-9.40107 EndY=-63.5 EndZ=0
    g1: LineSegment StartX=-9.40107 StartY=-63.5 StartZ=0 EndX=9.40108 EndY=-63.5 EndZ=0
    g2: LineSegment StartX=9.40108 StartY=-63.5 StartZ=0 EndX=9.40108 EndY=0 EndZ=0
    g3: LineSegment StartX=9.40108 StartY=0 StartZ=0 EndX=-9.40107 EndY=0 EndZ=0
  constraints (10):
    c: Coincident(g0,g1)
    c: Coincident(g1,g2)
    c: Coincident(g2,g3)
    c: Coincident(g3,g0)
    c: Vertical(g0)
    c: Vertical(g2)
    c: Horizontal(g1)
    c: Coincident(g0,g-6)
    c: Coincident(g-6,g2)
    c: DistanceY(g0,g0) = 63.5
FEATURE [PartDesign::Pocket] Pocket002
  BaseFeature = -> Pad004
  Direction = (0,-1,2e-16)
  Length = 17.5
  Length2 = 5
  Profile = -> Sketch010
  ReferenceAxis = -> Sketch010 [N_Axis]
  Refine = true
  Suppressed = false
  Type = 0
FEATURE [Sketcher::SketchObject] Sketch011
  ArcFitTolerance = 1e-06
  AttachmentSupport = -> [Pocket002]
  FullyConstrained = false
  MakeInternals = false
  MapMode = 5
  Placement = pos=(0,0,-2.2) rot=(1,0,0;3.14159rad)
  sketch-geometry (6):
    g0: LineSegment StartX=-52 StartY=120.048 StartZ=0 EndX=-52 EndY=95.0481 EndZ=0
    g1: LineSegment StartX=-52 StartY=95.0481 StartZ=0 EndX=52 EndY=95.0481 EndZ=0
    g2: LineSegment StartX=52 StartY=95.0481 StartZ=0 EndX=52 EndY=120.048 EndZ=0
    g3: LineSegment StartX=52 StartY=120.048 StartZ=0 EndX=-52 EndY=120.048 EndZ=0
    g4: GeomPoint X=1e-16 Y=120.048 Z=0
    g5: GeomPoint X=0 Y=105.469 Z=0
  constraints (13):
    c: Coincident(g0,g1)
    c: Coincident(g1,g2)
    c: Coincident(g2,g3)
    c: Coincident(g3,g0)
    c: Vertical(g0)
    c: Vertical(g2)
    c: Horizontal(g3)
    c: PointOnObject(g5,g-2)
    c: Symmetric(g0,g2,g4)
    c: Symmetric(g1,g0,g-2)
    c: DistanceY(g0,g0) = 25
    c: DistanceX(g3,g3) = 104
    c: Block(g3)
FEATURE [PartDesign::Pad] Pad005
  BaseFeature = -> Pocket002
  Direction = (0,0,-1)
  Length = 2.2
  Length2 = 10
  Profile = -> Sketch011
  ReferenceAxis = -> Sketch011 [N_Axis]
  Refine = true
  Suppressed = false
  Type = 0
  expr: Length = <<dimensies>>.DIKTE_FRONT
FEATURE [Sketcher::SketchObject] Sketch012
  ArcFitTolerance = 1e-06
  AttachmentSupport = -> [Pad005]
  FullyConstrained = true
  MakeInternals = false
  MapMode = 5
  sketch-geometry (5):
    g0: LineSegment StartX=-54.9901 StartY=-93.3363 StartZ=0 EndX=55.5099 EndY=-93.3363 EndZ=0
    g1: LineSegment StartX=-54.9901 StartY=-121.906 StartZ=0 EndX=55.5099 EndY=-121.906 EndZ=0
    g2: ArcOfCircle CenterX=-42.9824 CenterY=-107.621 CenterZ=0 NormalX=0 NormalY=0 NormalZ=1 AngleXU=0 Radius=18.6613 StartAngle=2.26979 EndAngle=4.01339
    g3: ArcOfCircle CenterX=42.9824 CenterY=-107.621 CenterZ=0 NormalX=0 NormalY=0 NormalZ=1 AngleXU=0 Radius=19 StartAngle=5.43233 EndAngle=7.13404
    g4: GeomPoint X=0 Y=-107.621 Z=0
  constraints (14):
    c: Horizontal(g0)
    c: Horizontal(g1)
    c: Coincident(g2,g0)
    c: Coincident(g2,g1)
    c: Coincident(g3,g0)
    c: Coincident(g3,g1)
    c: DistanceY(g1,g2) = 28.57
    c: DistanceX(g0,g0) = 110.5
    c: Horizontal(g3,g2)
    c: PointOnObject(g4,g-2)
    c: Symmetric(g2,g3,g4)
    c: Radius(g3) = 19
    c: Vertical(g1,g0)
    c: Block(g0)
FEATURE [PartDesign::Pad] Pad006
  BaseFeature = -> Pad005
  Direction = (0,0,1)
  Length = 8
  Length2 = 10
  Profile = -> Sketch012
  ReferenceAxis = -> Sketch012 [N_Axis]
  Refine = true
  Suppressed = false
  Type = 0
FEATURE [TechDraw::DrawSVGTemplate] Template
  EditableTexts = approval_person=B. Hecate,creator=A. Nemesis,date_of_issue=20/11/2024,document_type=Assembly Drawing,general_tolerances=ISO 2768-m,+7 more (map truncated)
  Height = 420
  Orientation = 1
  Template = <path>
  Width = 594
FEATURE [Sketcher::SketchObject] Sketch013
  ArcFitTolerance = 1e-06
  AttachmentSupport = -> [XY_Plane004]
  FullyConstrained = false
  MakeInternals = false
  MapMode = 5
  sketch-geometry (22):
    g0-g3: Circle [constr] x4 (B-spline internal-alignment scaffolding for g4; pole/knot coordinates omitted)
    g4: BSplineCurve PolesCount=14 KnotsCount=2 Degree=13 IsPeriodic=0
    g5: GeomPoint [constr] X=-690.982 Y=-223.281 Z=0
    g6: GeomPoint [constr] X=-657.619 Y=129.643 Z=0
    g7-g16: Circle [constr] x10 (B-spline internal-alignment scaffolding for g4; pole/knot coordinates omitted)
    g17: LineSegment StartX=-657.619 StartY=129.643 StartZ=0 EndX=-648.236 EndY=131.188 EndZ=0
    g18: LineSegment StartX=-648.236 StartY=131.188 StartZ=0 EndX=-626.176 EndY=6.08216 EndZ=0
    g19: LineSegment StartX=-626.176 StartY=6.08216 StartZ=0 EndX=-626.176 EndY=-236.32 EndZ=0
    g20: LineSegment StartX=-626.176 StartY=-236.32 StartZ=0 EndX=-690.982 EndY=-236.32 EndZ=0
    g21: LineSegment StartX=-690.982 StartY=-236.32 StartZ=0 EndX=-690.982 EndY=-223.281 EndZ=0
  constraints (37):
    c: Weight(g0) = 1
    c: Equal(g0,g1)
    c: Equal(g0,g2)
    c: Equal(g0,g3)
    c: InternalAlignment(g0-g3 -> g4) x4
    c: InternalAlignment(g5,g4)
    c: InternalAlignment(g6,g4)
    c: InternalAlignment(g7,g4)
    c: Equal(g7,g0)
    c: InternalAlignment(g8,g4)
    c: Equal(g8,g0)
    c: InternalAlignment(g9,g4)
    c: Equal(g9,g0)
    c: InternalAlignment(g10,g4)
    c: Equal(g10,g0)
    c: InternalAlignment(g11,g4)
    c: Equal(g11,g0)
    c: InternalAlignment(g12,g4)
    c: Equal(g12,g0)
    c: InternalAlignment(g13,g4)
    c: Equal(g13,g0)
    c: InternalAlignment(g14,g4)
    c: Equal(g14,g0)
    c: InternalAlignment(g15,g4)
    c: Equal(g15,g0)
    c: InternalAlignment(g16,g4)
    c: Equal(g16,g0)
    c: Coincident(g17,g4)
    c: Coincident(g18,g17)
    c: Coincident(g19,g18)
    c: Vertical(g19)
    c: Coincident(g20,g19)
    c: Horizontal(g20)
    c: Coincident(g21,g20)
    c: Coincident(g21,g4)
    c: Vertical(g21)
    c: Angle(g18,g19) = 2.96706
FEATURE [PartDesign::Pad] Pad007
  Direction = (0,0,1)
  Length = 44.45
  Length2 = 10
  Profile = -> Sketch013
  ReferenceAxis = -> Sketch013 [N_Axis]
  Refine = true
  Reversed = true
  Suppressed = false
  Type = 0
FEATURE [Sketcher::SketchObject] Sketch014
  ArcFitTolerance = 1e-06
  AttachmentSupport = -> [Pad007]
  ExternalGeometry = -> [Pad007]
  FullyConstrained = true
  MakeInternals = false
  MapMode = 5
  Placement = pos=(0,-236.32,0) rot=(1,0,0;1.5708rad)
  sketch-geometry (5):
    g0: LineSegment StartX=-626.176 StartY=-12.7 StartZ=0 EndX=-689.676 EndY=-12.7 EndZ=0
    g1: LineSegment StartX=-689.676 StartY=-12.7 StartZ=0 EndX=-689.676 EndY=-31.75 EndZ=0
    g2: LineSegment StartX=-689.676 StartY=-31.75 StartZ=0 EndX=-626.176 EndY=-31.75 EndZ=0
    g3: LineSegment StartX=-626.176 StartY=-31.75 StartZ=0 EndX=-626.176 EndY=-12.7 EndZ=0
    g4: GeomPoint X=-626.176 Y=-22.225 Z=0
  constraints (12):
    c: Coincident(g0,g1)
    c: Coincident(g1,g2)
    c: Coincident(g2,g3)
    c: Coincident(g3,g0)
    c: Horizontal(g0)
    c: Horizontal(g2)
    c: Vertical(g1)
    c: Vertical(g3)
    c: Symmetric(g3,g3,g4)
    c: Symmetric(g-3,g-4,g4)
    c: DistanceX(g0,g0) = 63.5
    c: DistanceY(g1,g1) = 19.05
FEATURE [PartDesign::Pad] Pad008
  BaseFeature = -> Pad007
  Direction = (0,-1,2e-16)
  Length = 15.875
  Length2 = 10
  Profile = -> Sketch014
  ReferenceAxis = -> Sketch014 [N_Axis]
  Refine = true
  Suppressed = false
  Type = 0
FEATURE [Sketcher::SketchObject] Sketch015
  ArcFitTolerance = 1e-06
  AttachmentSupport = -> [Pad006]
  ExternalGeometry = -> [Pad006]
  FullyConstrained = true
  MakeInternals = false
  MapMode = 5
  Placement = pos=(0,0,-67.8) rot=(1,0,0;3.14159rad)
  sketch-geometry (4):
    g0: LineSegment StartX=-9.32903 StartY=-91.8043 StartZ=0 EndX=9.40107 EndY=-91.8043 EndZ=0
    g1: LineSegment StartX=9.40107 StartY=-91.8043 StartZ=0 EndX=9.40107 EndY=-76.0875 EndZ=0
    g2: LineSegment StartX=9.40107 StartY=-76.0875 StartZ=0 EndX=-9.32903 EndY=-76.0875 EndZ=0
    g3: LineSegment StartX=-9.32903 StartY=-76.0875 StartZ=0 EndX=-9.32903 EndY=-91.8043 EndZ=0
  constraints (10):
    c: Coincident(g0,g1)
    c: Coincident(g1,g2)
    c: Coincident(g2,g3)
    c: Coincident(g3,g0)
    c: Horizontal(g0)
    c: Horizontal(g2)
    c: Vertical(g1)
    c: Vertical(g3)
    c: Coincident(g0,g-3)
    c: Coincident(g1,g-4)
FEATURE [PartDesign::Pad] Pad009
  BaseFeature = -> Pad006
  Direction = (0,0,-1)
  Length = 10
  Length2 = 10
  Profile = -> Sketch015
  ReferenceAxis = -> Sketch015 [N_Axis]
  Refine = true
  Reversed = true
  Suppressed = false
  Type = 3
  UpToFace = -> Pad006 [Face9]
FEATURE [Sketcher::SketchObject] Sketch016
  ArcFitTolerance = 1e-06
  AttachmentSupport = -> [Pad008]
  ExternalGeometry = -> [Pad008]
  FullyConstrained = true
  MakeInternals = false
  MapMode = 5
  Placement = pos=(-606.255,-106.899,0) rot=(0.510274,0.60812,0.60812;2.19793rad)
  sketch-geometry (13):
    g0: GeomPoint X=114.724 Y=-22.225 Z=0
    g1: GeomPoint X=114.724 Y=-6.35 Z=0
    g2: GeomPoint X=114.724 Y=-38.1 Z=0
    g3: LineSegment [constr] StartX=114.724 StartY=-6.35 StartZ=0 EndX=198.824 EndY=-6.35 EndZ=0
    g4: LineSegment [constr] StartX=114.724 StartY=-38.1 StartZ=0 EndX=198.824 EndY=-38.1 EndZ=0
    g5: GeomPoint [constr] X=160.724 Y=-6.35 Z=0
    g6: GeomPoint [constr] X=160.724 Y=-38.1 Z=0
    g7: LineSegment [constr] StartX=160.724 StartY=-6.35 StartZ=0 EndX=160.724 EndY=-38.1 EndZ=0
    g8: LineSegment [constr] StartX=198.824 StartY=-6.35 StartZ=0 EndX=198.824 EndY=-38.1 EndZ=0
    g9: Circle CenterX=198.824 CenterY=-6.35 CenterZ=0 NormalX=0 NormalY=0 NormalZ=1 AngleXU=0 Radius=4.76
    g10: Circle CenterX=160.724 CenterY=-6.35 CenterZ=0 NormalX=0 NormalY=0 NormalZ=1 AngleXU=0 Radius=4.76
    g11: Circle CenterX=198.824 CenterY=-38.1 CenterZ=0 NormalX=0 NormalY=0 NormalZ=1 AngleXU=0 Radius=4.76
    g12: Circle CenterX=160.724 CenterY=-38.1 CenterZ=0 NormalX=0 NormalY=0 NormalZ=1 AngleXU=0 Radius=4.76
  constraints (26):
    c: Symmetric(g-3,g-3,g0)
    c: PointOnObject(g1,g-3)
    c: Symmetric(g2,g1,g0)
    c: DistanceY(g2,g1) = 31.75
    c: Coincident(g3,g1)
    c: Horizontal(g3)
    c: Coincident(g4,g2)
    c: Horizontal(g4)
    c: PointOnObject(g5,g3)
    c: PointOnObject(g6,g4)
    c: Coincident(g7,g5)
    c: Coincident(g7,g6)
    c: Vertical(g7)
    c: Coincident(g8,g3)
    c: Coincident(g8,g4)
    c: Vertical(g8)
    c: DistanceX(g5,g1) = -46
    c: DistanceX(g3,g1) = -84.1
    c: Coincident(g9,g3)
    c: Coincident(g11,g4)
    c: Coincident(g12,g6)
    c: Equal(g9,g10)
    c: Equal(g10,g12)
    c: Equal(g12,g11)
    c: Diameter(g11) = 9.52
    c: Coincident(g10,g5)
FEATURE [Sketcher::SketchObject] Sketch017
  ArcFitTolerance = 1e-06
  AttachmentSupport = -> [Pad008]
  ExternalGeometry = -> [Pad008,Sketch016]
  FullyConstrained = false
  MakeInternals = false
  MapMode = 5
  Placement = pos=(-606.255,-106.899,0) rot=(0.510274,0.60812,0.60812;2.19793rad)
  sketch-geometry (15):
    g0: GeomPoint X=114.724 Y=-22.225 Z=0
    g1: GeomPoint X=114.724 Y=-3.97 Z=0
    g2: GeomPoint X=114.724 Y=-40.48 Z=0
    g3: LineSegment StartX=114.724 StartY=-3.97 StartZ=0 EndX=160.724 EndY=2.83375 EndZ=0
    g4: LineSegment StartX=114.724 StartY=-40.48 StartZ=0 EndX=160.724 EndY=-47.2838 EndZ=0
    g5: LineSegment [constr] StartX=160.724 StartY=2.83375 StartZ=0 EndX=160.724 EndY=-47.2838 EndZ=0
    g6: GeomPoint [constr] X=160.724 Y=-22.225 Z=0
    g7: LineSegment StartX=160.724 StartY=2.83375 StartZ=0 EndX=237.085 EndY=4.80349 EndZ=0
    g8: LineSegment StartX=160.724 StartY=-47.2838 StartZ=0 EndX=237.085 EndY=-49.2535 EndZ=0
    g9: GeomPoint X=241.76 Y=-22.225 Z=0
    g10: LineSegment [constr] StartX=237.085 StartY=4.80349 StartZ=0 EndX=237.085 EndY=-49.2535 EndZ=0
    g11: GeomPoint [constr] X=237.085 Y=-22.225 Z=0
    g12: ArcOfCircle CenterX=309.253 CenterY=3.368 CenterZ=0 NormalX=0 NormalY=0 NormalZ=1 AngleXU=0 Radius=72.1831 StartAngle=3.1217 EndAngle=3.50403
    g13: ArcOfCircle CenterX=309.253 CenterY=-47.818 CenterZ=0 NormalX=0 NormalY=0 NormalZ=1 AngleXU=0 Radius=72.1831 StartAngle=2.77915 EndAngle=3.16148
    g14: LineSegment StartX=114.724 StartY=-3.97 StartZ=0 EndX=114.724 EndY=-40.48 EndZ=0
  constraints (27):
    c: Symmetric(g-3,g-3,g0)
    c: PointOnObject(g1,g-3)
    c: Symmetric(g1,g2,g0)
    c: DistanceY(g2,g1) = 36.51
    c: Coincident(g3,g1)
    c: Coincident(g4,g2)
    c: Coincident(g5,g3)
    c: Coincident(g5,g4)
    c: Vertical(g5)
    c: Symmetric(g5,g5,g6)
    c: Symmetric(g-4,g-7,g6)
    c: Coincident(g7,g3)
    c: Coincident(g8,g4)
    c: Horizontal(g0,g9)
    c: Coincident(g10,g7)
    c: Coincident(g10,g8)
    c: Vertical(g10)
    c: Symmetric(g10,g10,g11)
    c: Horizontal(g11,g9)
    c: Coincident(g12,g7)
    c: Coincident(g12,g9)
    c: Coincident(g13,g9)
    c: Coincident(g13,g8)
    c: Equal(g13,g12)
    c: PointOnObject(g9,g-8)
    c: Coincident(g14,g1)
    c: Coincident(g14,g2)
FEATURE [Sketcher::SketchObject] Sketch018
  ArcFitTolerance = 1e-06
  AttachmentSupport = -> [Pad008]
  ExternalGeometry = -> [Pad008]
  FullyConstrained = true
  MakeInternals = false
  MapMode = 5
  Placement = pos=(-38.1526,231.663,0) rot=(-0.057741,0.705927,0.705927;3.25695rad)
  sketch-geometry (4):
    g0: LineSegment StartX=627.811 StartY=0 StartZ=0 EndX=616.865 EndY=0 EndZ=0
    g1: LineSegment StartX=616.865 StartY=0 StartZ=0 EndX=616.865 EndY=-44.45 EndZ=0
    g2: LineSegment StartX=616.865 StartY=-44.45 StartZ=0 EndX=627.811 EndY=-44.45 EndZ=0
    g3: LineSegment StartX=627.811 StartY=-44.45 StartZ=0 EndX=627.811 EndY=0 EndZ=0
  constraints (10):
    c: Coincident(g0,g1)
    c: Coincident(g1,g2)
    c: Coincident(g2,g3)
    c: Coincident(g3,g0)
    c: Horizontal(g0)
    c: Horizontal(g2)
    c: Vertical(g1)
    c: Vertical(g3)
    c: Coincident(g0,g-4)
    c: Coincident(g1,g-5)
FEATURE [PartDesign::Pocket] Pocket003
  BaseFeature = -> Pad008
  Direction = (0.162501,-0.986708,0)
  Length = 20
  Length2 = 5
  Profile = -> Sketch018
  ReferenceAxis = -> Sketch018 [N_Axis]
  Refine = true
  Suppressed = false
  Type = 0
FEATURE [PartDesign::Pad] Pad010
  BaseFeature = -> Pocket003
  Direction = (0.984808,0.173648,2e-16)
  Length = 12
  Length2 = 10
  Profile = -> Sketch017
  ReferenceAxis = -> Sketch017 [N_Axis]
  Refine = true
  Reversed = true
  Suppressed = false
  Type = 0
FEATURE [Sketcher::SketchObject] Sketch019
  ArcFitTolerance = 1e-06
  AttachmentSupport = -> [Pad010]
  ExternalGeometry = -> [Sketch017,Pad010]
  FullyConstrained = true
  MakeInternals = false
  MapMode = 5
  Placement = pos=(-606.255,-106.899,0) rot=(0.510274,0.60812,0.60812;2.19793rad)
  sketch-geometry (3):
    g0: LineSegment StartX=160.724 StartY=2.83375 StartZ=0 EndX=114.724 EndY=-3.97 EndZ=0
    g1: LineSegment StartX=114.724 StartY=-3.97 StartZ=0 EndX=-123.995 EndY=0 EndZ=0
    g2: LineSegment StartX=-123.995 StartY=0 StartZ=0 EndX=160.724 EndY=2.83375 EndZ=0
  constraints (6):
    c: Coincident(g-3,g0)
    c: Coincident(g0,g-3)
    c: Coincident(g0,g1)
    c: Coincident(g1,g-4)
    c: Coincident(g1,g2)
    c: Coincident(g2,g0)
FEATURE [PartDesign::Pocket] Pocket004
  BaseFeature = -> Pad010
  Direction = (-0.984808,-0.173648,0)
  Length = 500
  Length2 = 5
  Profile = -> Sketch019
  ReferenceAxis = -> Sketch019 [N_Axis]
  Refine = true
  Suppressed = false
  Type = 0
FEATURE [PartDesign::Hole] Hole
  BaseFeature = -> Pocket004
  CustomThreadClearance = 0
  Depth = 25
  DepthType = 0
  Diameter = 6
  DrillForDepth = false
  DrillPoint = 1
  DrillPointAngle = 118
  HoleCutCountersinkAngle = 90
  HoleCutCustomValues = false
  HoleCutDepth = 0
  HoleCutDiameter = 6.1
  HoleCutType = 0
  ModelThread = false
  Profile = -> Sketch016
  Refine = true
  Suppressed = false
  Tapered = false
  TaperedAngle = 90
  ThreadClass = 0
  ThreadDepth = 25
  ThreadDepthType = 0
  ThreadDirection = 0
  ThreadFit = 0
  ThreadSize = 0
  ThreadType = 0
  Threaded = false
  UseCustomThreadClearance = false
FEATURE [Sketcher::SketchObject] Sketch020
  ArcFitTolerance = 1e-06
  AttachmentSupport = -> [Hole]
  ExternalGeometry = -> [Sketch017,Hole]
  FullyConstrained = true
  MakeInternals = false
  MapMode = 5
  Placement = pos=(-606.255,-106.899,0) rot=(0.510274,0.60812,0.60812;2.19793rad)
  sketch-geometry (3):
    g0: LineSegment StartX=114.724 StartY=-40.48 StartZ=0 EndX=-123.995 EndY=-44.45 EndZ=0
    g1: LineSegment StartX=-123.995 StartY=-44.45 StartZ=0 EndX=160.724 EndY=-47.2838 EndZ=0
    g2: LineSegment StartX=160.724 StartY=-47.2838 StartZ=0 EndX=114.724 EndY=-40.48 EndZ=0
  constraints (6):
    c: Coincident(g-3,g0)
    c: Coincident(g0,g-4)
    c: Coincident(g0,g1)
    c: Coincident(g1,g-3)
    c: Coincident(g1,g2)
    c: Coincident(g2,g0)
FEATURE [PartDesign::Pocket] Pocket005
  BaseFeature = -> Hole
  Direction = (-0.984808,-0.173648,0)
  Length = 500
  Length2 = 5
  Profile = -> Sketch020
  ReferenceAxis = -> Sketch020 [N_Axis]
  Refine = true
  Suppressed = false
  Type = 0
FEATURE [Sketcher::SketchObject] Sketch021
  ArcFitTolerance = 1e-06
  AttachmentSupport = -> [Pocket005]
  ExternalGeometry = -> [Pocket005]
  FullyConstrained = true
  MakeInternals = false
  MapMode = 5
  Placement = pos=(-690.982,0,0) rot=(0.57735,-0.57735,-0.57735;2.0944rad)
  sketch-geometry (4):
    g0: LineSegment StartX=236.32 StartY=-0.187148 StartZ=0 EndX=223.281 EndY=-0.187148 EndZ=0
    g1: LineSegment StartX=223.281 StartY=-0.187148 StartZ=0 EndX=223.281 EndY=-44.0493 EndZ=0
    g2: LineSegment StartX=223.281 StartY=-44.0493 StartZ=0 EndX=236.32 EndY=-44.0493 EndZ=0
    g3: LineSegment StartX=236.32 StartY=-44.0493 StartZ=0 EndX=236.32 EndY=-0.187148 EndZ=0
  constraints (10):
    c: Coincident(g0,g1)
    c: Coincident(g1,g2)
    c: Coincident(g2,g3)
    c: Coincident(g3,g0)
    c: Horizontal(g0)
    c: Horizontal(g2)
    c: Vertical(g1)
    c: Vertical(g3)
    c: Coincident(g0,g-4)
    c: Coincident(g1,g-3)
FEATURE [PartDesign::Pad] Pad011
  BaseFeature = -> Pocket005
  Direction = (-1,0,0)
  Length = 2
  Length2 = 10
  Profile = -> Sketch021
  ReferenceAxis = -> Sketch021 [N_Axis]
  Refine = true
  Suppressed = false
  Type = 0
FEATURE [Sketcher::SketchObject] Sketch022
  ArcFitTolerance = 1e-06
  AttachmentSupport = -> [Pad011]
  ExternalGeometry = -> [Pad011,Sketch017]
  FullyConstrained = false
  MakeInternals = false
  MapMode = 5
  Placement = pos=(-626.176,0,0) rot=(0.57735,0.57735,0.57735;2.0944rad)
  sketch-geometry (7):
    g0: LineSegment StartX=2.91216 StartY=-3.91808 StartZ=0 EndX=-303.442 EndY=1.09931 EndZ=0
    g1: LineSegment StartX=2.91216 StartY=-40.5319 StartZ=0 EndX=-303.442 EndY=-45.5493 EndZ=0
    g2: GeomPoint X=-309.663 Y=-22.225 Z=0
    g3: GeomPoint X=6.08216 Y=-22.225 Z=0
    g4: ArcOfCircle CenterX=-336.111 CenterY=-2.67954 CenterZ=0 NormalX=0 NormalY=0 NormalZ=1 AngleXU=0 Radius=32.8871 StartAngle=5.64676 EndAngle=6.39834
    g5: ArcOfCircle CenterX=-336.111 CenterY=-41.7705 CenterZ=0 NormalX=0 NormalY=0 NormalZ=1 AngleXU=0 Radius=32.8871 StartAngle=6.16803 EndAngle=6.91961
    g6: LineSegment StartX=2.91216 StartY=-3.91808 StartZ=0 EndX=2.91216 EndY=-40.5319 EndZ=0
  constraints (16):
    c: PointOnObject(g-3,g0)
    c: PointOnObject(g-5,g1)
    c: Symmetric(g-4,g-4,g3)
    c: Horizontal(g3,g2)
    c: Vertical(g0,g1)
    c: Coincident(g4,g0)
    c: Coincident(g4,g2)
    c: Coincident(g5,g2)
    c: Coincident(g5,g1)
    c: Equal(g5,g4)
    c: PointOnObject(g0,g-3)
    c: PointOnObject(g1,g-5)
    c: Coincident(g6,g0)
    c: Coincident(g6,g1)
    c: Vertical(g6)
    c: DistanceX(g0,g-4) = 3.17
FEATURE [PartDesign::Pad] Pad012
  BaseFeature = -> Pad011
  Direction = (1,0,0)
  Length = 6.25
  Length2 = 10
  Profile = -> Sketch022
  ReferenceAxis = -> Sketch022 [N_Axis]
  Refine = true
  Suppressed = false
  Type = 0
FEATURE [Sketcher::SketchObject] Sketch023
  ArcFitTolerance = 1e-06
  AttachmentSupport = -> [Pad012]
  ExternalGeometry = -> [Pad012,Sketch017]
  FullyConstrained = true
  MakeInternals = false
  MapMode = 5
  Placement = pos=(-626.176,0,0) rot=(0.57735,0.57735,0.57735;2.0944rad)
  sketch-geometry (4):
    g0: LineSegment StartX=2.91216 StartY=-3.91808 StartZ=0 EndX=2.91216 EndY=-40.5319 EndZ=0
    g1: LineSegment StartX=2.91216 StartY=-40.5319 StartZ=0 EndX=6.08216 EndY=-40.48 EndZ=0
    g2: LineSegment StartX=6.08216 StartY=-40.48 StartZ=0 EndX=6.08216 EndY=-3.97 EndZ=0
    g3: LineSegment StartX=6.08216 StartY=-3.97 StartZ=0 EndX=2.91216 EndY=-3.91808 EndZ=0
  constraints (8):
    c: Coincident(g-3,g0)
    c: Coincident(g0,g-3)
    c: Coincident(g0,g1)
    c: Coincident(g1,g-4)
    c: Coincident(g1,g2)
    c: Coincident(g2,g-4)
    c: Coincident(g2,g3)
    c: Coincident(g3,g0)
FEATURE [PartDesign::Pad] Pad013
  BaseFeature = -> Pad012
  Direction = (1,0,0)
  Length = 9
  Length2 = 10
  Profile = -> Sketch023
  ReferenceAxis = -> Sketch023 [N_Axis]
  Refine = true
  Suppressed = false
  Type = 0
FEATURE [PartDesign::Body] Body002
  AllowCompound = false
  Group = -> [Sketch013,Pad007,Sketch014,Pad008,Sketch016,Sketch017,Sketch018,Pocket003,Pad010,Sketch019,Pocket004,Hole,Sketch020,Pocket005,Sketch021,Pad011,Sketch022,Pad012,Sketch023,Pad013]
  Origin = -> Origin004
  Tip = -> Pad013
FEATURE [App::Part] Part001  label="neck"
  Group = -> [Body002]
  Origin = -> Origin003
FEATURE [App::Link] neck  label="neck001"
  LinkPlacement = pos=(33,54,166) rot=(0,0,1;0rad)
  LinkedObject = -> Part001
  Placement = pos=(33,54,166) rot=(0,0,1;0rad)
FEATURE [App::FeaturePython] GroundedJoint  # Assembly grounded joint (typed FeaturePython)
  ObjectToGround = -> neck
  Placement = pos=(33,54,166) rot=(0,0,1;0rad)
FEATURE [App::Link] kast  label="kast001"
  LinkPlacement = pos=(-593.176,-273.72,143.775) rot=(0,1,0;1.5708rad)
  LinkedObject = -> Part
  Placement = pos=(-593.176,-273.72,143.775) rot=(0,1,0;1.5708rad)
FEATURE [App::FeaturePython] Joint  label="Distance"  # Assembly joint (typed FeaturePython)
  Activated = true
  AngleMax = 0
  AngleMin = 0
  Detach1 = false
  Detach2 = false
  Distance = 0
  Distance2 = 0
  EnableAngleMax = false
  EnableAngleMin = false
  EnableLengthMax = false
  EnableLengthMin = false
  JointType = 5 (Distance)
  LengthMax = 0
  LengthMin = 0
  Placement1 = pos=(-657.926,-252.195,-22.225) rot=(0.57735,0.57735,0.57735;4.18879rad)
  Placement2 = pos=(-3e-16,75.525,-35) rot=(0,0.707107,0.707107;3.14159rad)
  Reference1 = -> Assembly [neck.Body002.Face33,neck.Body002.Face33]
  Reference2 = -> Assembly [kast.Body001.Face22,kast.Body001.Face22]
FEATURE [App::FeaturePython] Joint001  label="Distance001"  # Assembly joint (typed FeaturePython)
  Activated = true
  AngleMax = 0
  AngleMin = 0
  Detach1 = false
  Detach2 = false
  Distance = 0
  Distance2 = 0
  EnableAngleMax = false
  EnableAngleMin = false
  EnableLengthMax = false
  EnableLengthMin = false
  JointType = 5 (Distance)
  LengthMax = 0
  LengthMin = 0
  Placement1 = pos=(-0.0143885,-72.8993,0) rot=(0,0,1;0rad)
  Placement2 = pos=(-626.176,-273.803,-22.225) rot=(0.707107,0,0.707107;3.14159rad)
  Reference1 = -> Assembly [kast.Body001.Face4,kast.Body001.Vertex14]
  Reference2 = -> Assembly [neck.Body002.Face26,neck.Body002.Vertex50]
FEATURE [App::FeaturePython] Joint002  label="Distance002"  # Assembly joint (typed FeaturePython)
  Activated = true
  AngleMax = 0
  AngleMin = 0
  Detach1 = false
  Detach2 = false
  Distance = 0
  Distance2 = 0
  EnableAngleMax = false
  EnableAngleMin = false
  EnableLengthMax = false
  EnableLengthMin = false
  JointType = 5 (Distance)
  LengthMax = 0
  LengthMin = 0
  Placement1 = pos=(-657.926,-244.257,-12.7) rot=(0,1,0;3.14159rad)
  Placement2 = pos=(-9.525,83.6605,-35) rot=(0.57735,0.57735,0.57735;2.0944rad)
  Reference1 = -> Assembly [neck.Body002.Face31,neck.Body002.Vertex56]
  Reference2 = -> Assembly [kast.Body001.Face23,kast.Body001.Face23]
FEATURE [Assembly::JointGroup] Joints
  Group = -> [GroundedJoint,Joint,Joint001,Joint002]
FEATURE [Assembly::AssemblyObject] Assembly
  Group = -> [Joints,neck,GroundedJoint,kast,Joint,Joint001,Joint002]
  Origin = -> Origin005
  Type = Assembly
FEATURE [Sketcher::SketchObject] Sketch024  label="vk001"
  ArcFitTolerance = 1e-06
  FullyConstrained = false
  MakeInternals = false
  sketch-geometry (68):
    g0: BSplineCurve PolesCount=33 KnotsCount=31 Degree=3 IsPeriodic=0
    g1-g33: Circle [constr] x33 (B-spline internal-alignment scaffolding for g0; pole/knot coordinates omitted)
    g34-g64: GeomPoint [constr] x31 (B-spline internal-alignment scaffolding for g0; pole/knot coordinates omitted)
    g65: BSplineCurve PolesCount=33 KnotsCount=31 Degree=3 IsPeriodic=0
    g66: LineSegment StartX=-9.40108 StartY=93.5875 StartZ=0 EndX=9.40107 EndY=93.5875 EndZ=0
    g67: LineSegment StartX=-0.637124 StartY=-210.927 StartZ=0 EndX=0.637124 EndY=-210.927 EndZ=0
  constraints (73):
    c: InternalAlignment(g1,g0)
    c: Weight(g1) = 1
    c: InternalAlignment(g2,g0)
    c: Equal(g2,g1)
    c: InternalAlignment(g3,g0)
    c: Equal(g3,g1)
    c: InternalAlignment(g4,g0)
    c: Equal(g4,g1)
    c: InternalAlignment(g5,g0)
    c: Equal(g5,g1)
    c: InternalAlignment(g6,g0)
    c: Equal(g6,g1)
    c: InternalAlignment(g7,g0)
    c: Equal(g7,g1)
    c: InternalAlignment(g8,g0)
    c: Equal(g8,g1)
    c: InternalAlignment(g9,g0)
    c: Equal(g9,g1)
    c: InternalAlignment(g10,g0)
    c: Equal(g10,g1)
    c: InternalAlignment(g11,g0)
    c: Equal(g11,g1)
    c: InternalAlignment(g12,g0)
    c: Equal(g12,g1)
    c: InternalAlignment(g13,g0)
    c: Equal(g13,g1)
    c: InternalAlignment(g14,g0)
    c: Equal(g14,g1)
    c: InternalAlignment(g15,g0)
    c: Equal(g15,g1)
    c: InternalAlignment(g16,g0)
    c: Equal(g16,g1)
    c: InternalAlignment(g17,g0)
    c: Equal(g17,g1)
    c: InternalAlignment(g18,g0)
    c: Equal(g18,g1)
    c: InternalAlignment(g19,g0)
    c: Equal(g19,g1)
    c: InternalAlignment(g20,g0)
    c: Equal(g20,g1)
    c: InternalAlignment(g21,g0)
    c: Equal(g21,g1)
    c: InternalAlignment(g22,g0)
    c: Equal(g22,g1)
    c: InternalAlignment(g23,g0)
    c: Equal(g23,g1)
    c: InternalAlignment(g24,g0)
    c: Equal(g24,g1)
    c: InternalAlignment(g25,g0)
    c: Equal(g25,g1)
    c: InternalAlignment(g26,g0)
    c: Equal(g26,g1)
    c: InternalAlignment(g27,g0)
    c: Equal(g27,g1)
    c: InternalAlignment(g28,g0)
    c: Equal(g28,g1)
    c: InternalAlignment(g29,g0)
    c: Equal(g29,g1)
    c: InternalAlignment(g30,g0)
    c: Equal(g30,g1)
    c: InternalAlignment(g31,g0)
    c: Equal(g31,g1)
    c: InternalAlignment(g32,g0)
    c: Equal(g32,g1)
    c: InternalAlignment(g33,g0)
    c: Equal(g33,g1)
    c: InternalAlignment(g34-g64 -> g0) x31
    c: Coincident(g66,g0)
    c: Coincident(g66,g65)
    c: Horizontal(g66)
    c: Coincident(g67,g0)
    c: Coincident(g67,g65)
    c: Horizontal(g67)
FEATURE [PartDesign::Pad] Pad014
  Direction = (0,0,1)
  Length = 2.2
  Length2 = 10
  Profile = -> Sketch024
  ReferenceAxis = -> Sketch024 [N_Axis]
  Reversed = true
  Suppressed = false
  Type = 0
  expr: Length = <<dimensies001>>.DIKTE_FRONT
FEATURE [Sketcher::SketchObject] Sketch025
  ArcFitTolerance = 1e-06
  AttachmentSupport = -> [XY_Plane006]
  FullyConstrained = true
  MakeInternals = false
  MapMode = 5
  sketch-geometry (1):
    g0: Circle CenterX=0 CenterY=0 CenterZ=0 NormalX=0 NormalY=0 NormalZ=1 AngleXU=0 Radius=32.5435
  constraints (2):
    c: Coincident(g0,g-1)
    c: Diameter(g0) = 65.087
FEATURE [PartDesign::Pocket] Pocket006
  BaseFeature = -> Pad014
  Direction = (0,0,-1)
  Length = 5
  Length2 = 5
  Profile = -> Sketch025
  ReferenceAxis = -> Sketch025 [N_Axis]
  Suppressed = false
  Type = 2
FEATURE [Sketcher::SketchObject] Sketch026  label="base sketch002"
  ArcFitTolerance = 1e-06
  FullyConstrained = false
  MakeInternals = false
  sketch-geometry (136):
    g0: BSplineCurve PolesCount=33 KnotsCount=31 Degree=3 IsPeriodic=0
    g1-g33: Circle [constr] x33 (B-spline internal-alignment scaffolding for g0; pole/knot coordinates omitted)
    g34-g64: GeomPoint [constr] x31 (B-spline internal-alignment scaffolding for g0; pole/knot coordinates omitted)
    g65: BSplineCurve PolesCount=33 KnotsCount=31 Degree=3 IsPeriodic=0
    g66-g98: Circle [constr] x33 (B-spline internal-alignment scaffolding for g65; pole/knot coordinates omitted)
    g99-g129: GeomPoint [constr] x31 (B-spline internal-alignment scaffolding for g65; pole/knot coordinates omitted)
    g130: BSplineCurve PolesCount=33 KnotsCount=31 Degree=3 IsPeriodic=0
    g131: BSplineCurve PolesCount=33 KnotsCount=31 Degree=3 IsPeriodic=0
    g132: LineSegment StartX=-9.32903 StartY=91.8043 StartZ=0 EndX=9.32903 EndY=91.8043 EndZ=0
    g133: LineSegment StartX=-9.40108 StartY=93.5875 StartZ=0 EndX=9.40107 EndY=93.5875 EndZ=0
    g134: LineSegment StartX=-0.629425 StartY=-209.143 StartZ=0 EndX=0.629425 EndY=-209.143 EndZ=0
    g135: LineSegment StartX=-0.637124 StartY=-210.927 StartZ=0 EndX=0.637124 EndY=-210.927 EndZ=0
  constraints (146):
    c: InternalAlignment(g1,g0)
    c: Weight(g1) = 1
    c: InternalAlignment(g2,g0)
    c: Equal(g2,g1)
    c: InternalAlignment(g3,g0)
    c: Equal(g3,g1)
    c: InternalAlignment(g4,g0)
    c: Equal(g4,g1)
    c: InternalAlignment(g5,g0)
    c: Equal(g5,g1)
    c: InternalAlignment(g6,g0)
    c: Equal(g6,g1)
    c: InternalAlignment(g7,g0)
    c: Equal(g7,g1)
    c: InternalAlignment(g8,g0)
    c: Equal(g8,g1)
    c: InternalAlignment(g9,g0)
    c: Equal(g9,g1)
    c: InternalAlignment(g10,g0)
    c: Equal(g10,g1)
    c: InternalAlignment(g11,g0)
    c: Equal(g11,g1)
    c: InternalAlignment(g12,g0)
    c: Equal(g12,g1)
    c: InternalAlignment(g13,g0)
    c: Equal(g13,g1)
    c: InternalAlignment(g14,g0)
    c: Equal(g14,g1)
    c: InternalAlignment(g15,g0)
    c: Equal(g15,g1)
    c: InternalAlignment(g16,g0)
    c: Equal(g16,g1)
    c: InternalAlignment(g17,g0)
    c: Equal(g17,g1)
    c: InternalAlignment(g18,g0)
    c: Equal(g18,g1)
    c: InternalAlignment(g19,g0)
    c: Equal(g19,g1)
    c: InternalAlignment(g20,g0)
    c: Equal(g20,g1)
    c: InternalAlignment(g21,g0)
    c: Equal(g21,g1)
    c: InternalAlignment(g22,g0)
    c: Equal(g22,g1)
    c: InternalAlignment(g23,g0)
    c: Equal(g23,g1)
    c: InternalAlignment(g24,g0)
    c: Equal(g24,g1)
    c: InternalAlignment(g25,g0)
    c: Equal(g25,g1)
    c: InternalAlignment(g26,g0)
    c: Equal(g26,g1)
    c: InternalAlignment(g27,g0)
    c: Equal(g27,g1)
    c: InternalAlignment(g28,g0)
    c: Equal(g28,g1)
    c: InternalAlignment(g29,g0)
    c: Equal(g29,g1)
    c: InternalAlignment(g30,g0)
    c: Equal(g30,g1)
    c: InternalAlignment(g31,g0)
    c: Equal(g31,g1)
    c: InternalAlignment(g32,g0)
    c: Equal(g32,g1)
    c: InternalAlignment(g33,g0)
    c: Equal(g33,g1)
    c: InternalAlignment(g34-g64 -> g0) x31
    c: InternalAlignment(g66,g65)
    c: Weight(g66) = 1
    c: InternalAlignment(g67,g65)
    c: Equal(g67,g66)
    c: InternalAlignment(g68,g65)
    c: Equal(g68,g66)
    c: InternalAlignment(g69,g65)
    c: Equal(g69,g66)
    c: InternalAlignment(g70,g65)
    c: Equal(g70,g66)
    c: InternalAlignment(g71,g65)
    c: Equal(g71,g66)
    c: InternalAlignment(g72,g65)
    c: Equal(g72,g66)
    c: InternalAlignment(g73,g65)
    c: Equal(g73,g66)
    c: InternalAlignment(g74,g65)
    c: Equal(g74,g66)
    c: InternalAlignment(g75,g65)
    c: Equal(g75,g66)
    c: InternalAlignment(g76,g65)
    c: Equal(g76,g66)
    c: InternalAlignment(g77,g65)
    c: Equal(g77,g66)
    c: InternalAlignment(g78,g65)
    c: Equal(g78,g66)
    c: InternalAlignment(g79,g65)
    c: Equal(g79,g66)
    c: InternalAlignment(g80,g65)
    c: Equal(g80,g66)
    c: InternalAlignment(g81,g65)
    c: Equal(g81,g66)
    c: InternalAlignment(g82,g65)
    c: Equal(g82,g66)
    c: InternalAlignment(g83,g65)
    c: Equal(g83,g66)
    c: InternalAlignment(g84,g65)
    c: Equal(g84,g66)
    c: InternalAlignment(g85,g65)
    c: Equal(g85,g66)
    c: InternalAlignment(g86,g65)
    c: Equal(g86,g66)
    c: InternalAlignment(g87,g65)
    c: Equal(g87,g66)
    c: InternalAlignment(g88,g65)
    c: Equal(g88,g66)
    c: InternalAlignment(g89,g65)
    c: Equal(g89,g66)
    c: InternalAlignment(g90,g65)
    c: Equal(g90,g66)
    c: InternalAlignment(g91,g65)
    c: Equal(g91,g66)
    c: InternalAlignment(g92,g65)
    c: Equal(g92,g66)
    c: InternalAlignment(g93,g65)
    c: Equal(g93,g66)
    c: InternalAlignment(g94,g65)
    c: Equal(g94,g66)
    c: InternalAlignment(g95,g65)
    c: Equal(g95,g66)
    c: InternalAlignment(g96,g65)
    c: Equal(g96,g66)
    c: InternalAlignment(g97,g65)
    c: Equal(g97,g66)
    c: InternalAlignment(g98,g65)
    c: Equal(g98,g66)
    c: InternalAlignment(g99-g129 -> g65) x31
    c: Coincident(g132,g65)
    c: Coincident(g132,g131)
    c: Horizontal(g132)
    c: Coincident(g133,g0)
    c: Coincident(g133,g130)
    c: Horizontal(g133)
    c: Coincident(g134,g65)
    c: Coincident(g134,g131)
    c: Horizontal(g134)
    c: Coincident(g135,g0)
    c: Coincident(g135,g130)
    c: Horizontal(g135)
FEATURE [PartDesign::Pad] Pad015
  BaseFeature = -> Pocket006
  Direction = (0,0,1)
  Length = 70
  Length2 = 10
  Profile = -> Sketch026
  ReferenceAxis = -> Sketch026 [N_Axis]
  Refine = true
  Reversed = true
  Suppressed = false
  Type = 0
  expr: Length = 70
FEATURE [Sketcher::SketchObject] Sketch027
  ArcFitTolerance = 1e-06
  AttachmentSupport = -> [YZ_Plane006]
  ExternalGeometry = -> [Pad015]
  FullyConstrained = true
  MakeInternals = false
  MapMode = 5
  Placement = pos=(0,0,0) rot=(0.57735,0.57735,0.57735;2.0944rad)
  sketch-geometry (10):
    g0: GeomPoint X=0 Y=-2.2 Z=0
    g1: GeomPoint X=-44.45 Y=-2.2 Z=0
    g2: GeomPoint X=44.45 Y=-2.2 Z=0
    g3: LineSegment StartX=-47.625 StartY=-2.2 StartZ=0 EndX=-41.275 EndY=-2.2 EndZ=0
    g4: LineSegment StartX=-41.275 StartY=-2.2 StartZ=0 EndX=-41.275 EndY=-7.2 EndZ=0
    g5: LineSegment StartX=-41.275 StartY=-7.2 StartZ=0 EndX=-42.45 EndY=-11.725 EndZ=0
    g6: LineSegment StartX=-42.45 StartY=-11.725 StartZ=0 EndX=-46.45 EndY=-11.725 EndZ=0
    g7: LineSegment StartX=-46.45 StartY=-11.725 StartZ=0 EndX=-47.625 EndY=-7.2 EndZ=0
    g8: LineSegment StartX=-47.625 StartY=-7.2 StartZ=0 EndX=-47.625 EndY=-2.2 EndZ=0
    g9: GeomPoint X=-44.45 Y=-11.725 Z=0
  constraints (24):
    c: PointOnObject(g0,g-4)
    c: PointOnObject(g1,g-4)
    c: DistanceX(g1,g0) = 44.45
    c: Symmetric(g1,g2,g0)
    c: PointOnObject(g0,g-2)
    c: PointOnObject(g3,g-4)
    c: PointOnObject(g3,g-4)
    c: Coincident(g3,g4)
    c: Vertical(g4)
    c: Coincident(g4,g5)
    c: Coincident(g5,g6)
    c: Horizontal(g6)
    c: Coincident(g6,g7)
    c: Coincident(g7,g8)
    c: Coincident(g8,g3)
    c: Symmetric(g3,g3,g1)
    c: Vertical(g8)
    c: DistanceX(g3,g3) = 6.35
    c: Horizontal(g4,g7)
    c: DistanceY(g5,g3) = 9.525
    c: DistanceY(g8,g8) = 5
    c: Symmetric(g6,g6,g9)
    c: Vertical(g9,g1)
    c: DistanceX(g6,g9) = 2
FEATURE [PartDesign::Pad] Pad016
  BaseFeature = -> Pad015
  Direction = (1,0,0)
  Length = 155
  Length2 = 10
  Midplane = true
  Profile = -> Sketch027
  ReferenceAxis = -> Sketch027 [N_Axis]
  Refine = true
  Suppressed = false
  Type = 0
FEATURE [Sketcher::SketchObject] Sketch028
  ArcFitTolerance = 1e-06
  AttachmentSupport = -> [Pad016]
  ExternalGeometry = -> [Pad016]
  FullyConstrained = true
  MakeInternals = false
  MapMode = 5
  Placement = pos=(0,-41.275,0) rot=(0,0.707107,0.707107;3.14159rad)
  sketch-geometry (12):
    g0: GeomPoint X=40 Y=-11.725 Z=0
    g1: GeomPoint X=-40 Y=-11.725 Z=0
    g2: GeomPoint X=0 Y=-7.2 Z=0
    g3: GeomPoint X=-78.3882 Y=-4.2 Z=0
    g4: GeomPoint X=78.3882 Y=-4.2 Z=0
    g5: LineSegment StartX=78.3882 StartY=-4.2 StartZ=0 EndX=40 EndY=-11.725 EndZ=0
    g6: LineSegment StartX=-40 StartY=-11.725 StartZ=0 EndX=-78.3882 EndY=-4.2 EndZ=0
    g7: LineSegment StartX=40 StartY=-11.725 StartZ=0 EndX=-40 EndY=-11.725 EndZ=0
    g8: LineSegment StartX=78.3882 StartY=-4.2 StartZ=0 EndX=78.3882 EndY=-24.2 EndZ=0
    g9: LineSegment StartX=78.3882 StartY=-24.2 StartZ=0 EndX=-78.3882 EndY=-24.2 EndZ=0
    g10: LineSegment StartX=-78.3882 StartY=-4.2 StartZ=0 EndX=-78.3882 EndY=-24.2 EndZ=0
    g11: GeomPoint X=0 Y=-11.725 Z=0
  constraints (24):
    c: Symmetric(g-4,g-4,g2)
    c: PointOnObject(g3,g-6)
    c: PointOnObject(g4,g-5)
    c: Horizontal(g4,g3)
    c: DistanceX(g2,g0) = 40
    c: Coincident(g5,g4)
    c: Coincident(g5,g0)
    c: Coincident(g6,g1)
    c: DistanceY(g4,g-5) = 2
    c: Coincident(g7,g0)
    c: Coincident(g7,g1)
    c: Coincident(g8,g4)
    c: Vertical(g8)
    c: Coincident(g9,g8)
    c: Horizontal(g9)
    c: Coincident(g10,g9)
    c: Vertical(g10)
    c: DistanceY(g10,g10) = 20
    c: Coincident(g3,g10)
    c: Coincident(g3,g6)
    c: PointOnObject(g11,g-7)
    c: PointOnObject(g11,g-2)
    c: Symmetric(g1,g0,g11)
    c: Horizontal(g7)
FEATURE [PartDesign::Pocket] Pocket007
  BaseFeature = -> Pad016
  Direction = (0,-1,2e-16)
  Length = 9
  Length2 = 5
  Profile = -> Sketch028
  ReferenceAxis = -> Sketch028 [N_Axis]
  Refine = true
  Suppressed = false
  Type = 0
FEATURE [Sketcher::SketchObject] Sketch029
  ArcFitTolerance = 1e-06
  AttachmentSupport = -> [Pocket007]
  ExternalGeometry = -> [Pocket007]
  FullyConstrained = true
  MakeInternals = false
  MapMode = 5
  Placement = pos=(0,0,-2.2) rot=(1,0,0;3.14159rad)
  sketch-geometry (8):
    g0: LineSegment StartX=-25 StartY=209.143 StartZ=0 EndX=25 EndY=209.143 EndZ=0
    g1: GeomPoint X=-2.2048e-07 Y=209.143 Z=0
    g2: LineSegment StartX=-25 StartY=209.143 StartZ=0 EndX=-25 EndY=201.143 EndZ=0
    g3: LineSegment StartX=-25 StartY=201.143 StartZ=0 EndX=-20 EndY=196.143 EndZ=0
    g4: LineSegment StartX=-20 StartY=196.143 StartZ=0 EndX=20 EndY=196.143 EndZ=0
    g5: LineSegment StartX=20 StartY=196.143 StartZ=0 EndX=25 EndY=201.143 EndZ=0
    g6: LineSegment StartX=25 StartY=201.143 StartZ=0 EndX=25 EndY=209.143 EndZ=0
    g7: GeomPoint X=0 Y=196.143 Z=0
  constraints (19):
    c: Horizontal(g0)
    c: Symmetric(g0,g0,g1)
    c: Symmetric(g-4,g-3,g1)
    c: DistanceX(g0,g0) = 50
    c: Coincident(g0,g2)
    c: Vertical(g2)
    c: Coincident(g2,g3)
    c: Coincident(g3,g4)
    c: Horizontal(g4)
    c: Coincident(g4,g5)
    c: Coincident(g5,g6)
    c: Coincident(g6,g0)
    c: Vertical(g6)
    c: Symmetric(g4,g4,g7)
    c: PointOnObject(g7,g-2)
    c: Angle(g3,g2) = 2.35619
    c: DistanceY(g6,g6) = 8
    c: DistanceX(g4,g4) = 40
    c: Horizontal(g2,g5)
FEATURE [PartDesign::Pad] Pad017
  BaseFeature = -> Pocket007
  Direction = (0,0,-1)
  Length = 65.6
  Length2 = 10
  Profile = -> Sketch029
  ReferenceAxis = -> Sketch029 [N_Axis]
  Refine = true
  Suppressed = false
  Type = 0
  expr: Length = <<dimensies001>>.DIEPTE - 2 * <<dimensies001>>.DIKTE_FRONT
FEATURE [Sketcher::SketchObject] Sketch030
  ArcFitTolerance = 1e-06
  AttachmentSupport = -> [Pad017]
  FullyConstrained = true
  MakeInternals = false
  MapMode = 5
  Placement = pos=(0,0,-2.2) rot=(1,0,0;3.14159rad)
  sketch-geometry (12):
    g0: LineSegment StartX=-25.4 StartY=-92.925 StartZ=0 EndX=-25.4 EndY=-68.289 EndZ=0
    g1: LineSegment StartX=-25.4 StartY=-68.289 StartZ=0 EndX=-19.036 EndY=-61.925 EndZ=0
    g2: LineSegment StartX=-19.036 StartY=-61.925 StartZ=0 EndX=19.036 EndY=-61.925 EndZ=0
    g3: LineSegment StartX=19.036 StartY=-61.925 StartZ=0 EndX=25.4 EndY=-68.289 EndZ=0
    g4: LineSegment StartX=25.4 StartY=-68.289 StartZ=0 EndX=25.4 EndY=-92.925 EndZ=0
    g5: LineSegment StartX=25.4 StartY=-92.925 StartZ=0 EndX=9.525 EndY=-92.925 EndZ=0
    g6: LineSegment StartX=9.525 StartY=-92.925 StartZ=0 EndX=9.525 EndY=-75.525 EndZ=0
    g7: LineSegment StartX=9.525 StartY=-75.525 StartZ=0 EndX=-9.525 EndY=-75.525 EndZ=0
    g8: LineSegment StartX=-9.525 StartY=-75.525 StartZ=0 EndX=-9.525 EndY=-92.925 EndZ=0
    g9: LineSegment StartX=-9.525 StartY=-92.925 StartZ=0 EndX=-25.4 EndY=-92.925 EndZ=0
    g10: GeomPoint X=0 Y=-61.925 Z=0
    g11: GeomPoint X=0 Y=-75.525 Z=0
  constraints (32):
    c: Vertical(g0)
    c: Coincident(g0,g1)
    c: Coincident(g1,g2)
    c: Horizontal(g2)
    c: Coincident(g2,g3)
    c: Coincident(g3,g4)
    c: Vertical(g4)
    c: Coincident(g4,g5)
    c: Horizontal(g5)
    c: Coincident(g5,g6)
    c: Vertical(g6)
    c: Coincident(g6,g7)
    c: Horizontal(g7)
    c: Coincident(g7,g8)
    c: Vertical(g8)
    c: Coincident(g8,g9)
    c: Coincident(g9,g0)
    c: Horizontal(g9)
    c: Symmetric(g2,g2,g10)
    c: Symmetric(g7,g7,g11)
    c: PointOnObject(g11,g-2)
    c: PointOnObject(g10,g-2)
    c: Angle(g0,g1) = 2.35619
    c: Horizontal(g3,g0)
    c: Equal(g9,g5)
    c: DistanceX(g8,g5) = 19.05
    c: DistanceY(g0,g1) = 31
    c: DistanceY(g8,g8) = 17.4
    c: Horizontal(g8,g5)
    c: DistanceX(g0,g4) = 50.8
    c: Distance(g1,g1) = 9
    c: Block(g2)
FEATURE [PartDesign::Pad] Pad018
  BaseFeature = -> Pad017
  Direction = (0,0,-1)
  Length = 65.6
  Length2 = 10
  Profile = -> Sketch030
  ReferenceAxis = -> Sketch030 [N_Axis]
  Refine = true
  Suppressed = false
  Type = 0
  expr: Length = <<dimensies001>>.DIEPTE - 2 * <<dimensies001>>.DIKTE_FRONT
FEATURE [Sketcher::SketchObject] Sketch031
  ArcFitTolerance = 1e-06
  AttachmentSupport = -> [Pad018]
  ExternalGeometry = -> [Pad018,Sketch024]
  FullyConstrained = true
  MakeInternals = false
  MapMode = 5
  Placement = pos=(0,93.5875,0) rot=(0,0.707107,0.707107;3.14159rad)
  sketch-geometry (4):
    g0: LineSegment StartX=-9.40107 StartY=0 StartZ=0 EndX=-9.40107 EndY=-63.5 EndZ=0
    g1: LineSegment StartX=-9.40107 StartY=-63.5 StartZ=0 EndX=9.40108 EndY=-63.5 EndZ=0
    g2: LineSegment StartX=9.40108 StartY=-63.5 StartZ=0 EndX=9.40108 EndY=0 EndZ=0
    g3: LineSegment StartX=9.40108 StartY=0 StartZ=0 EndX=-9.40107 EndY=0 EndZ=0
  constraints (10):
    c: Coincident(g0,g1)
    c: Coincident(g1,g2)
    c: Coincident(g2,g3)
    c: Coincident(g3,g0)
    c: Vertical(g0)
    c: Vertical(g2)
    c: Horizontal(g1)
    c: Coincident(g0,g-6)
    c: Coincident(g-6,g2)
    c: DistanceY(g0,g0) = 63.5
FEATURE [PartDesign::Pocket] Pocket008
  BaseFeature = -> Pad018
  Direction = (0,-1,2e-16)
  Length = 17.5
  Length2 = 5
  Profile = -> Sketch031
  ReferenceAxis = -> Sketch031 [N_Axis]
  Refine = true
  Suppressed = false
  Type = 0
FEATURE [Sketcher::SketchObject] Sketch032
  ArcFitTolerance = 1e-06
  AttachmentSupport = -> [Pocket008]
  FullyConstrained = false
  MakeInternals = false
  MapMode = 5
  Placement = pos=(0,0,-2.2) rot=(1,0,0;3.14159rad)
  sketch-geometry (6):
    g0: LineSegment StartX=-52 StartY=120.048 StartZ=0 EndX=-52 EndY=95.0481 EndZ=0
    g1: LineSegment StartX=-52 StartY=95.0481 StartZ=0 EndX=52 EndY=95.0481 EndZ=0
    g2: LineSegment StartX=52 StartY=95.0481 StartZ=0 EndX=52 EndY=120.048 EndZ=0
    g3: LineSegment StartX=52 StartY=120.048 StartZ=0 EndX=-52 EndY=120.048 EndZ=0
    g4: GeomPoint X=1e-16 Y=120.048 Z=0
    g5: GeomPoint X=0 Y=105.469 Z=0
  constraints (13):
    c: Coincident(g0,g1)
    c: Coincident(g1,g2)
    c: Coincident(g2,g3)
    c: Coincident(g3,g0)
    c: Vertical(g0)
    c: Vertical(g2)
    c: Horizontal(g3)
    c: PointOnObject(g5,g-2)
    c: Symmetric(g0,g2,g4)
    c: Symmetric(g1,g0,g-2)
    c: DistanceY(g0,g0) = 25
    c: DistanceX(g3,g3) = 104
    c: Block(g3)
FEATURE [PartDesign::Pad] Pad019
  BaseFeature = -> Pocket008
  Direction = (0,0,-1)
  Length = 2.2
  Length2 = 10
  Profile = -> Sketch032
  ReferenceAxis = -> Sketch032 [N_Axis]
  Refine = true
  Suppressed = false
  Type = 0
  expr: Length = <<dimensies001>>.DIKTE_FRONT
FEATURE [Sketcher::SketchObject] Sketch033
  ArcFitTolerance = 1e-06
  AttachmentSupport = -> [Pad019]
  FullyConstrained = true
  MakeInternals = false
  MapMode = 5
  sketch-geometry (5):
    g0: LineSegment StartX=-54.9901 StartY=-93.3363 StartZ=0 EndX=55.5099 EndY=-93.3363 EndZ=0
    g1: LineSegment StartX=-54.9901 StartY=-121.906 StartZ=0 EndX=55.5099 EndY=-121.906 EndZ=0
    g2: ArcOfCircle CenterX=-42.9824 CenterY=-107.621 CenterZ=0 NormalX=0 NormalY=0 NormalZ=1 AngleXU=0 Radius=18.6613 StartAngle=2.26979 EndAngle=4.01339
    g3: ArcOfCircle CenterX=42.9824 CenterY=-107.621 CenterZ=0 NormalX=0 NormalY=0 NormalZ=1 AngleXU=0 Radius=19 StartAngle=5.43233 EndAngle=7.13404
    g4: GeomPoint X=0 Y=-107.621 Z=0
  constraints (14):
    c: Horizontal(g0)
    c: Horizontal(g1)
    c: Coincident(g2,g0)
    c: Coincident(g2,g1)
    c: Coincident(g3,g0)
    c: Coincident(g3,g1)
    c: DistanceY(g1,g2) = 28.57
    c: DistanceX(g0,g0) = 110.5
    c: Horizontal(g3,g2)
    c: PointOnObject(g4,g-2)
    c: Symmetric(g2,g3,g4)
    c: Radius(g3) = 19
    c: Vertical(g1,g0)
    c: Block(g0)
FEATURE [PartDesign::Pad] Pad020
  BaseFeature = -> Pad019
  Direction = (0,0,1)
  Length = 8
  Length2 = 10
  Profile = -> Sketch033
  ReferenceAxis = -> Sketch033 [N_Axis]
  Refine = true
  Suppressed = false
  Type = 0
FEATURE [Sketcher::SketchObject] Sketch034
  ArcFitTolerance = 1e-06
  AttachmentSupport = -> [Pad020]
  ExternalGeometry = -> [Pad020]
  FullyConstrained = true
  MakeInternals = false
  MapMode = 5
  Placement = pos=(0,0,-67.8) rot=(1,0,0;3.14159rad)
  sketch-geometry (4):
    g0: LineSegment StartX=-9.32903 StartY=-91.8043 StartZ=0 EndX=9.40107 EndY=-91.8043 EndZ=0
    g1: LineSegment StartX=9.40107 StartY=-91.8043 StartZ=0 EndX=9.40107 EndY=-76.0875 EndZ=0
    g2: LineSegment StartX=9.40107 StartY=-76.0875 StartZ=0 EndX=-9.32903 EndY=-76.0875 EndZ=0
    g3: LineSegment StartX=-9.32903 StartY=-76.0875 StartZ=0 EndX=-9.32903 EndY=-91.8043 EndZ=0
  constraints (10):
    c: Coincident(g0,g1)
    c: Coincident(g1,g2)
    c: Coincident(g2,g3)
    c: Coincident(g3,g0)
    c: Horizontal(g0)
    c: Horizontal(g2)
    c: Vertical(g1)
    c: Vertical(g3)
    c: Coincident(g0,g-3)
    c: Coincident(g1,g-4)
FEATURE [PartDesign::Pad] Pad021
  BaseFeature = -> Pad020
  Direction = (0,0,-1)
  Length = 10
  Length2 = 10
  Profile = -> Sketch034
  ReferenceAxis = -> Sketch034 [N_Axis]
  Refine = true
  Reversed = true
  Suppressed = false
  Type = 3
  UpToFace = -> Pad020 [Face9]
FEATURE [PartDesign::Body] Body003
  AllowCompound = false
  Group = -> [Sketch024,Pad014,Sketch025,Pocket006,Sketch026,Pad015,Sketch027,Pad016,Sketch028,Pocket007,Sketch029,Pad017,Sketch030,Pad018,Sketch031,Pocket008,Sketch032,Pad019,Sketch033,Pad020,Sketch034,Pad021]
  Origin = -> Origin012
  Tip = -> Pad021
FEATURE [TechDraw::DrawProjGroupItem] ProjItem002  label="Left001"
  CoarseView = false
  Direction = (-1e-16,-1e-16,-1)
  Focus = 100
  HardHidden = false
  IsoCount = 0
  IsoHidden = false
  IsoVisible = false
  LockPosition = false
  Perspective = false
  Rotation = 0
  RotationVector = (1,0,0)
  ScaleType = 0
  ScrubCount = 1
  SeamHidden = false
  SeamVisible = false
  SmoothHidden = false
  SmoothVisible = true
  Source = -> [Body003]
  Type = 1
  X = 207.14
  XDirection = (0,-1,1e-16)
  Y = 0
FEATURE [Spreadsheet::Sheet] Spreadsheet001  label="dimensies001"
  cells = A3='dikte front; B3(DIKTE_FRONT)=2.2; C3='mm; A4='diepte; B4(DIEPTE)=70
FEATURE [Sketcher::SketchObject] Sketch035  label="vk002"
  ArcFitTolerance = 1e-06
  FullyConstrained = false
  MakeInternals = false
  sketch-geometry (68):
    g0: BSplineCurve PolesCount=33 KnotsCount=31 Degree=3 IsPeriodic=0
    g1-g33: Circle [constr] x33 (B-spline internal-alignment scaffolding for g0; pole/knot coordinates omitted)
    g34-g64: GeomPoint [constr] x31 (B-spline internal-alignment scaffolding for g0; pole/knot coordinates omitted)
    g65: BSplineCurve PolesCount=33 KnotsCount=31 Degree=3 IsPeriodic=0
    g66: LineSegment StartX=-9.40108 StartY=93.5875 StartZ=0 EndX=9.40107 EndY=93.5875 EndZ=0
    g67: LineSegment StartX=-0.637124 StartY=-210.927 StartZ=0 EndX=0.637124 EndY=-210.927 EndZ=0
  constraints (73):
    c: InternalAlignment(g1,g0)
    c: Weight(g1) = 1
    c: InternalAlignment(g2,g0)
    c: Equal(g2,g1)
    c: InternalAlignment(g3,g0)
    c: Equal(g3,g1)
    c: InternalAlignment(g4,g0)
    c: Equal(g4,g1)
    c: InternalAlignment(g5,g0)
    c: Equal(g5,g1)
    c: InternalAlignment(g6,g0)
    c: Equal(g6,g1)
    c: InternalAlignment(g7,g0)
    c: Equal(g7,g1)
    c: InternalAlignment(g8,g0)
    c: Equal(g8,g1)
    c: InternalAlignment(g9,g0)
    c: Equal(g9,g1)
    c: InternalAlignment(g10,g0)
    c: Equal(g10,g1)
    c: InternalAlignment(g11,g0)
    c: Equal(g11,g1)
    c: InternalAlignment(g12,g0)
    c: Equal(g12,g1)
    c: InternalAlignment(g13,g0)
    c: Equal(g13,g1)
    c: InternalAlignment(g14,g0)
    c: Equal(g14,g1)
    c: InternalAlignment(g15,g0)
    c: Equal(g15,g1)
    c: InternalAlignment(g16,g0)
    c: Equal(g16,g1)
    c: InternalAlignment(g17,g0)
    c: Equal(g17,g1)
    c: InternalAlignment(g18,g0)
    c: Equal(g18,g1)
    c: InternalAlignment(g19,g0)
    c: Equal(g19,g1)
    c: InternalAlignment(g20,g0)
    c: Equal(g20,g1)
    c: InternalAlignment(g21,g0)
    c: Equal(g21,g1)
    c: InternalAlignment(g22,g0)
    c: Equal(g22,g1)
    c: InternalAlignment(g23,g0)
    c: Equal(g23,g1)
    c: InternalAlignment(g24,g0)
    c: Equal(g24,g1)
    c: InternalAlignment(g25,g0)
    c: Equal(g25,g1)
    c: InternalAlignment(g26,g0)
    c: Equal(g26,g1)
    c: InternalAlignment(g27,g0)
    c: Equal(g27,g1)
    c: InternalAlignment(g28,g0)
    c: Equal(g28,g1)
    c: InternalAlignment(g29,g0)
    c: Equal(g29,g1)
    c: InternalAlignment(g30,g0)
    c: Equal(g30,g1)
    c: InternalAlignment(g31,g0)
    c: Equal(g31,g1)
    c: InternalAlignment(g32,g0)
    c: Equal(g32,g1)
    c: InternalAlignment(g33,g0)
    c: Equal(g33,g1)
    c: InternalAlignment(g34-g64 -> g0) x31
    c: Coincident(g66,g0)
    c: Coincident(g66,g65)
    c: Horizontal(g66)
    c: Coincident(g67,g0)
    c: Coincident(g67,g65)
    c: Horizontal(g67)
FEATURE [PartDesign::Pad] Pad022
  Direction = (0,0,1)
  Length = 2.2
  Length2 = 10
  Profile = -> Sketch035
  ReferenceAxis = -> Sketch035 [N_Axis]
  Reversed = true
  Suppressed = false
  Type = 0
  expr: Length = <<dimensies002>>.DIKTE_FRONT
FEATURE [Sketcher::SketchObject] Sketch036
  ArcFitTolerance = 1e-06
  AttachmentSupport = -> [XY_Plane007]
  FullyConstrained = true
  MakeInternals = false
  MapMode = 5
  sketch-geometry (1):
    g0: Circle CenterX=0 CenterY=0 CenterZ=0 NormalX=0 NormalY=0 NormalZ=1 AngleXU=0 Radius=32.5435
  constraints (2):
    c: Coincident(g0,g-1)
    c: Diameter(g0) = 65.087
FEATURE [PartDesign::Pocket] Pocket009
  BaseFeature = -> Pad022
  Direction = (0,0,-1)
  Length = 5
  Length2 = 5
  Profile = -> Sketch036
  ReferenceAxis = -> Sketch036 [N_Axis]
  Suppressed = false
  Type = 2
FEATURE [Sketcher::SketchObject] Sketch037  label="base sketch003"
  ArcFitTolerance = 1e-06
  FullyConstrained = false
  MakeInternals = false
  sketch-geometry (136):
    g0: BSplineCurve PolesCount=33 KnotsCount=31 Degree=3 IsPeriodic=0
    g1-g33: Circle [constr] x33 (B-spline internal-alignment scaffolding for g0; pole/knot coordinates omitted)
    g34-g64: GeomPoint [constr] x31 (B-spline internal-alignment scaffolding for g0; pole/knot coordinates omitted)
    g65: BSplineCurve PolesCount=33 KnotsCount=31 Degree=3 IsPeriodic=0
    g66-g98: Circle [constr] x33 (B-spline internal-alignment scaffolding for g65; pole/knot coordinates omitted)
    g99-g129: GeomPoint [constr] x31 (B-spline internal-alignment scaffolding for g65; pole/knot coordinates omitted)
    g130: BSplineCurve PolesCount=33 KnotsCount=31 Degree=3 IsPeriodic=0
    g131: BSplineCurve PolesCount=33 KnotsCount=31 Degree=3 IsPeriodic=0
    g132: LineSegment StartX=-9.32903 StartY=91.8043 StartZ=0 EndX=9.32903 EndY=91.8043 EndZ=0
    g133: LineSegment StartX=-9.40108 StartY=93.5875 StartZ=0 EndX=9.40107 EndY=93.5875 EndZ=0
    g134: LineSegment StartX=-0.629425 StartY=-209.143 StartZ=0 EndX=0.629425 EndY=-209.143 EndZ=0
    g135: LineSegment StartX=-0.637124 StartY=-210.927 StartZ=0 EndX=0.637124 EndY=-210.927 EndZ=0
  constraints (146):
    c: InternalAlignment(g1,g0)
    c: Weight(g1) = 1
    c: InternalAlignment(g2,g0)
    c: Equal(g2,g1)
    c: InternalAlignment(g3,g0)
    c: Equal(g3,g1)
    c: InternalAlignment(g4,g0)
    c: Equal(g4,g1)
    c: InternalAlignment(g5,g0)
    c: Equal(g5,g1)
    c: InternalAlignment(g6,g0)
    c: Equal(g6,g1)
    c: InternalAlignment(g7,g0)
    c: Equal(g7,g1)
    c: InternalAlignment(g8,g0)
    c: Equal(g8,g1)
    c: InternalAlignment(g9,g0)
    c: Equal(g9,g1)
    c: InternalAlignment(g10,g0)
    c: Equal(g10,g1)
    c: InternalAlignment(g11,g0)
    c: Equal(g11,g1)
    c: InternalAlignment(g12,g0)
    c: Equal(g12,g1)
    c: InternalAlignment(g13,g0)
    c: Equal(g13,g1)
    c: InternalAlignment(g14,g0)
    c: Equal(g14,g1)
    c: InternalAlignment(g15,g0)
    c: Equal(g15,g1)
    c: InternalAlignment(g16,g0)
    c: Equal(g16,g1)
    c: InternalAlignment(g17,g0)
    c: Equal(g17,g1)
    c: InternalAlignment(g18,g0)
    c: Equal(g18,g1)
    c: InternalAlignment(g19,g0)
    c: Equal(g19,g1)
    c: InternalAlignment(g20,g0)
    c: Equal(g20,g1)
    c: InternalAlignment(g21,g0)
    c: Equal(g21,g1)
    c: InternalAlignment(g22,g0)
    c: Equal(g22,g1)
    c: InternalAlignment(g23,g0)
    c: Equal(g23,g1)
    c: InternalAlignment(g24,g0)
    c: Equal(g24,g1)
    c: InternalAlignment(g25,g0)
    c: Equal(g25,g1)
    c: InternalAlignment(g26,g0)
    c: Equal(g26,g1)
    c: InternalAlignment(g27,g0)
    c: Equal(g27,g1)
    c: InternalAlignment(g28,g0)
    c: Equal(g28,g1)
    c: InternalAlignment(g29,g0)
    c: Equal(g29,g1)
    c: InternalAlignment(g30,g0)
    c: Equal(g30,g1)
    c: InternalAlignment(g31,g0)
    c: Equal(g31,g1)
    c: InternalAlignment(g32,g0)
    c: Equal(g32,g1)
    c: InternalAlignment(g33,g0)
    c: Equal(g33,g1)
    c: InternalAlignment(g34-g64 -> g0) x31
    c: InternalAlignment(g66,g65)
    c: Weight(g66) = 1
    c: InternalAlignment(g67,g65)
    c: Equal(g67,g66)
    c: InternalAlignment(g68,g65)
    c: Equal(g68,g66)
    c: InternalAlignment(g69,g65)
    c: Equal(g69,g66)
    c: InternalAlignment(g70,g65)
    c: Equal(g70,g66)
    c: InternalAlignment(g71,g65)
    c: Equal(g71,g66)
    c: InternalAlignment(g72,g65)
    c: Equal(g72,g66)
    c: InternalAlignment(g73,g65)
    c: Equal(g73,g66)
    c: InternalAlignment(g74,g65)
    c: Equal(g74,g66)
    c: InternalAlignment(g75,g65)
    c: Equal(g75,g66)
    c: InternalAlignment(g76,g65)
    c: Equal(g76,g66)
    c: InternalAlignment(g77,g65)
    c: Equal(g77,g66)
    c: InternalAlignment(g78,g65)
    c: Equal(g78,g66)
    c: InternalAlignment(g79,g65)
    c: Equal(g79,g66)
    c: InternalAlignment(g80,g65)
    c: Equal(g80,g66)
    c: InternalAlignment(g81,g65)
    c: Equal(g81,g66)
    c: InternalAlignment(g82,g65)
    c: Equal(g82,g66)
    c: InternalAlignment(g83,g65)
    c: Equal(g83,g66)
    c: InternalAlignment(g84,g65)
    c: Equal(g84,g66)
    c: InternalAlignment(g85,g65)
    c: Equal(g85,g66)
    c: InternalAlignment(g86,g65)
    c: Equal(g86,g66)
    c: InternalAlignment(g87,g65)
    c: Equal(g87,g66)
    c: InternalAlignment(g88,g65)
    c: Equal(g88,g66)
    c: InternalAlignment(g89,g65)
    c: Equal(g89,g66)
    c: InternalAlignment(g90,g65)
    c: Equal(g90,g66)
    c: InternalAlignment(g91,g65)
    c: Equal(g91,g66)
    c: InternalAlignment(g92,g65)
    c: Equal(g92,g66)
    c: InternalAlignment(g93,g65)
    c: Equal(g93,g66)
    c: InternalAlignment(g94,g65)
    c: Equal(g94,g66)
    c: InternalAlignment(g95,g65)
    c: Equal(g95,g66)
    c: InternalAlignment(g96,g65)
    c: Equal(g96,g66)
    c: InternalAlignment(g97,g65)
    c: Equal(g97,g66)
    c: InternalAlignment(g98,g65)
    c: Equal(g98,g66)
    c: InternalAlignment(g99-g129 -> g65) x31
    c: Coincident(g132,g65)
    c: Coincident(g132,g131)
    c: Horizontal(g132)
    c: Coincident(g133,g0)
    c: Coincident(g133,g130)
    c: Horizontal(g133)
    c: Coincident(g134,g65)
    c: Coincident(g134,g131)
    c: Horizontal(g134)
    c: Coincident(g135,g0)
    c: Coincident(g135,g130)
    c: Horizontal(g135)
FEATURE [PartDesign::Pad] Pad023
  BaseFeature = -> Pocket009
  Direction = (0,0,1)
  Length = 70
  Length2 = 10
  Profile = -> Sketch037
  ReferenceAxis = -> Sketch037 [N_Axis]
  Refine = true
  Reversed = true
  Suppressed = false
  Type = 0
  expr: Length = 70
FEATURE [Sketcher::SketchObject] Sketch038
  ArcFitTolerance = 1e-06
  AttachmentSupport = -> [YZ_Plane007]
  ExternalGeometry = -> [Pad023]
  FullyConstrained = true
  MakeInternals = false
  MapMode = 5
  Placement = pos=(0,0,0) rot=(0.57735,0.57735,0.57735;2.0944rad)
  sketch-geometry (10):
    g0: GeomPoint X=0 Y=-2.2 Z=0
    g1: GeomPoint X=-44.45 Y=-2.2 Z=0
    g2: GeomPoint X=44.45 Y=-2.2 Z=0
    g3: LineSegment StartX=-47.625 StartY=-2.2 StartZ=0 EndX=-41.275 EndY=-2.2 EndZ=0
    g4: LineSegment StartX=-41.275 StartY=-2.2 StartZ=0 EndX=-41.275 EndY=-7.2 EndZ=0
    g5: LineSegment StartX=-41.275 StartY=-7.2 StartZ=0 EndX=-42.45 EndY=-11.725 EndZ=0
    g6: LineSegment StartX=-42.45 StartY=-11.725 StartZ=0 EndX=-46.45 EndY=-11.725 EndZ=0
    g7: LineSegment StartX=-46.45 StartY=-11.725 StartZ=0 EndX=-47.625 EndY=-7.2 EndZ=0
    g8: LineSegment StartX=-47.625 StartY=-7.2 StartZ=0 EndX=-47.625 EndY=-2.2 EndZ=0
    g9: GeomPoint X=-44.45 Y=-11.725 Z=0
  constraints (24):
    c: PointOnObject(g0,g-4)
    c: PointOnObject(g1,g-4)
    c: DistanceX(g1,g0) = 44.45
    c: Symmetric(g1,g2,g0)
    c: PointOnObject(g0,g-2)
    c: PointOnObject(g3,g-4)
    c: PointOnObject(g3,g-4)
    c: Coincident(g3,g4)
    c: Vertical(g4)
    c: Coincident(g4,g5)
    c: Coincident(g5,g6)
    c: Horizontal(g6)
    c: Coincident(g6,g7)
    c: Coincident(g7,g8)
    c: Coincident(g8,g3)
    c: Symmetric(g3,g3,g1)
    c: Vertical(g8)
    c: DistanceX(g3,g3) = 6.35
    c: Horizontal(g4,g7)
    c: DistanceY(g5,g3) = 9.525
    c: DistanceY(g8,g8) = 5
    c: Symmetric(g6,g6,g9)
    c: Vertical(g9,g1)
    c: DistanceX(g6,g9) = 2
FEATURE [PartDesign::Pad] Pad024
  BaseFeature = -> Pad023
  Direction = (1,0,0)
  Length = 155
  Length2 = 10
  Midplane = true
  Profile = -> Sketch038
  ReferenceAxis = -> Sketch038 [N_Axis]
  Refine = true
  Suppressed = false
  Type = 0
FEATURE [Sketcher::SketchObject] Sketch039
  ArcFitTolerance = 1e-06
  AttachmentSupport = -> [Pad024]
  ExternalGeometry = -> [Pad024]
  FullyConstrained = true
  MakeInternals = false
  MapMode = 5
  Placement = pos=(0,-41.275,0) rot=(0,0.707107,0.707107;3.14159rad)
  sketch-geometry (12):
    g0: GeomPoint X=40 Y=-11.725 Z=0
    g1: GeomPoint X=-40 Y=-11.725 Z=0
    g2: GeomPoint X=0 Y=-7.2 Z=0
    g3: GeomPoint X=-78.3882 Y=-4.2 Z=0
    g4: GeomPoint X=78.3882 Y=-4.2 Z=0
    g5: LineSegment StartX=78.3882 StartY=-4.2 StartZ=0 EndX=40 EndY=-11.725 EndZ=0
    g6: LineSegment StartX=-40 StartY=-11.725 StartZ=0 EndX=-78.3882 EndY=-4.2 EndZ=0
    g7: LineSegment StartX=40 StartY=-11.725 StartZ=0 EndX=-40 EndY=-11.725 EndZ=0
    g8: LineSegment StartX=78.3882 StartY=-4.2 StartZ=0 EndX=78.3882 EndY=-24.2 EndZ=0
    g9: LineSegment StartX=78.3882 StartY=-24.2 StartZ=0 EndX=-78.3882 EndY=-24.2 EndZ=0
    g10: LineSegment StartX=-78.3882 StartY=-4.2 StartZ=0 EndX=-78.3882 EndY=-24.2 EndZ=0
    g11: GeomPoint X=0 Y=-11.725 Z=0
  constraints (24):
    c: Symmetric(g-4,g-4,g2)
    c: PointOnObject(g3,g-6)
    c: PointOnObject(g4,g-5)
    c: Horizontal(g4,g3)
    c: DistanceX(g2,g0) = 40
    c: Coincident(g5,g4)
    c: Coincident(g5,g0)
    c: Coincident(g6,g1)
    c: DistanceY(g4,g-5) = 2
    c: Coincident(g7,g0)
    c: Coincident(g7,g1)
    c: Coincident(g8,g4)
    c: Vertical(g8)
    c: Coincident(g9,g8)
    c: Horizontal(g9)
    c: Coincident(g10,g9)
    c: Vertical(g10)
    c: DistanceY(g10,g10) = 20
    c: Coincident(g3,g10)
    c: Coincident(g3,g6)
    c: PointOnObject(g11,g-7)
    c: PointOnObject(g11,g-2)
    c: Symmetric(g1,g0,g11)
    c: Horizontal(g7)
FEATURE [PartDesign::Pocket] Pocket010
  BaseFeature = -> Pad024
  Direction = (0,-1,2e-16)
  Length = 9
  Length2 = 5
  Profile = -> Sketch039
  ReferenceAxis = -> Sketch039 [N_Axis]
  Refine = true
  Suppressed = false
  Type = 0
FEATURE [Sketcher::SketchObject] Sketch040
  ArcFitTolerance = 1e-06
  AttachmentSupport = -> [Pocket010]
  ExternalGeometry = -> [Pocket010]
  FullyConstrained = true
  MakeInternals = false
  MapMode = 5
  Placement = pos=(0,0,-2.2) rot=(1,0,0;3.14159rad)
  sketch-geometry (8):
    g0: LineSegment StartX=-25 StartY=209.143 StartZ=0 EndX=25 EndY=209.143 EndZ=0
    g1: GeomPoint X=-2.2048e-07 Y=209.143 Z=0
    g2: LineSegment StartX=-25 StartY=209.143 StartZ=0 EndX=-25 EndY=201.143 EndZ=0
    g3: LineSegment StartX=-25 StartY=201.143 StartZ=0 EndX=-20 EndY=196.143 EndZ=0
    g4: LineSegment StartX=-20 StartY=196.143 StartZ=0 EndX=20 EndY=196.143 EndZ=0
    g5: LineSegment StartX=20 StartY=196.143 StartZ=0 EndX=25 EndY=201.143 EndZ=0
    g6: LineSegment StartX=25 StartY=201.143 StartZ=0 EndX=25 EndY=209.143 EndZ=0
    g7: GeomPoint X=0 Y=196.143 Z=0
  constraints (19):
    c: Horizontal(g0)
    c: Symmetric(g0,g0,g1)
    c: Symmetric(g-4,g-3,g1)
    c: DistanceX(g0,g0) = 50
    c: Coincident(g0,g2)
    c: Vertical(g2)
    c: Coincident(g2,g3)
    c: Coincident(g3,g4)
    c: Horizontal(g4)
    c: Coincident(g4,g5)
    c: Coincident(g5,g6)
    c: Coincident(g6,g0)
    c: Vertical(g6)
    c: Symmetric(g4,g4,g7)
    c: PointOnObject(g7,g-2)
    c: Angle(g3,g2) = 2.35619
    c: DistanceY(g6,g6) = 8
    c: DistanceX(g4,g4) = 40
    c: Horizontal(g2,g5)
FEATURE [PartDesign::Pad] Pad025
  BaseFeature = -> Pocket010
  Direction = (0,0,-1)
  Length = 65.6
  Length2 = 10
  Profile = -> Sketch040
  ReferenceAxis = -> Sketch040 [N_Axis]
  Refine = true
  Suppressed = false
  Type = 0
  expr: Length = <<dimensies002>>.DIEPTE - 2 * <<dimensies002>>.DIKTE_FRONT
FEATURE [Sketcher::SketchObject] Sketch041
  ArcFitTolerance = 1e-06
  AttachmentSupport = -> [Pad025]
  FullyConstrained = true
  MakeInternals = false
  MapMode = 5
  Placement = pos=(0,0,-2.2) rot=(1,0,0;3.14159rad)
  sketch-geometry (12):
    g0: LineSegment StartX=-25.4 StartY=-92.925 StartZ=0 EndX=-25.4 EndY=-68.289 EndZ=0
    g1: LineSegment StartX=-25.4 StartY=-68.289 StartZ=0 EndX=-19.036 EndY=-61.925 EndZ=0
    g2: LineSegment StartX=-19.036 StartY=-61.925 StartZ=0 EndX=19.036 EndY=-61.925 EndZ=0
    g3: LineSegment StartX=19.036 StartY=-61.925 StartZ=0 EndX=25.4 EndY=-68.289 EndZ=0
    g4: LineSegment StartX=25.4 StartY=-68.289 StartZ=0 EndX=25.4 EndY=-92.925 EndZ=0
    g5: LineSegment StartX=25.4 StartY=-92.925 StartZ=0 EndX=9.525 EndY=-92.925 EndZ=0
    g6: LineSegment StartX=9.525 StartY=-92.925 StartZ=0 EndX=9.525 EndY=-75.525 EndZ=0
    g7: LineSegment StartX=9.525 StartY=-75.525 StartZ=0 EndX=-9.525 EndY=-75.525 EndZ=0
    g8: LineSegment StartX=-9.525 StartY=-75.525 StartZ=0 EndX=-9.525 EndY=-92.925 EndZ=0
    g9: LineSegment StartX=-9.525 StartY=-92.925 StartZ=0 EndX=-25.4 EndY=-92.925 EndZ=0
    g10: GeomPoint X=0 Y=-61.925 Z=0
    g11: GeomPoint X=0 Y=-75.525 Z=0
  constraints (32):
    c: Vertical(g0)
    c: Coincident(g0,g1)
    c: Coincident(g1,g2)
    c: Horizontal(g2)
    c: Coincident(g2,g3)
    c: Coincident(g3,g4)
    c: Vertical(g4)
    c: Coincident(g4,g5)
    c: Horizontal(g5)
    c: Coincident(g5,g6)
    c: Vertical(g6)
    c: Coincident(g6,g7)
    c: Horizontal(g7)
    c: Coincident(g7,g8)
    c: Vertical(g8)
    c: Coincident(g8,g9)
    c: Coincident(g9,g0)
    c: Horizontal(g9)
    c: Symmetric(g2,g2,g10)
    c: Symmetric(g7,g7,g11)
    c: PointOnObject(g11,g-2)
    c: PointOnObject(g10,g-2)
    c: Angle(g0,g1) = 2.35619
    c: Horizontal(g3,g0)
    c: Equal(g9,g5)
    c: DistanceX(g8,g5) = 19.05
    c: DistanceY(g0,g1) = 31
    c: DistanceY(g8,g8) = 17.4
    c: Horizontal(g8,g5)
    c: DistanceX(g0,g4) = 50.8
    c: Distance(g1,g1) = 9
    c: Block(g2)
FEATURE [PartDesign::Pad] Pad026
  BaseFeature = -> Pad025
  Direction = (0,0,-1)
  Length = 65.6
  Length2 = 10
  Profile = -> Sketch041
  ReferenceAxis = -> Sketch041 [N_Axis]
  Refine = true
  Suppressed = false
  Type = 0
  expr: Length = <<dimensies002>>.DIEPTE - 2 * <<dimensies002>>.DIKTE_FRONT
FEATURE [Sketcher::SketchObject] Sketch042
  ArcFitTolerance = 1e-06
  AttachmentSupport = -> [Pad026]
  ExternalGeometry = -> [Pad026,Sketch035]
  FullyConstrained = true
  MakeInternals = false
  MapMode = 5
  Placement = pos=(0,93.5875,0) rot=(0,0.707107,0.707107;3.14159rad)
  sketch-geometry (4):
    g0: LineSegment StartX=-9.40107 StartY=0 StartZ=0 EndX=-9.40107 EndY=-63.5 EndZ=0
    g1: LineSegment StartX=-9.40107 StartY=-63.5 StartZ=0 EndX=9.40108 EndY=-63.5 EndZ=0
    g2: LineSegment StartX=9.40108 StartY=-63.5 StartZ=0 EndX=9.40108 EndY=0 EndZ=0
    g3: LineSegment StartX=9.40108 StartY=0 StartZ=0 EndX=-9.40107 EndY=0 EndZ=0
  constraints (10):
    c: Coincident(g0,g1)
    c: Coincident(g1,g2)
    c: Coincident(g2,g3)
    c: Coincident(g3,g0)
    c: Vertical(g0)
    c: Vertical(g2)
    c: Horizontal(g1)
    c: Coincident(g0,g-6)
    c: Coincident(g-6,g2)
    c: DistanceY(g0,g0) = 63.5
FEATURE [PartDesign::Pocket] Pocket011
  BaseFeature = -> Pad026
  Direction = (0,-1,2e-16)
  Length = 17.5
  Length2 = 5
  Profile = -> Sketch042
  ReferenceAxis = -> Sketch042 [N_Axis]
  Refine = true
  Suppressed = false
  Type = 0
FEATURE [Sketcher::SketchObject] Sketch043
  ArcFitTolerance = 1e-06
  AttachmentSupport = -> [Pocket011]
  FullyConstrained = false
  MakeInternals = false
  MapMode = 5
  Placement = pos=(0,0,-2.2) rot=(1,0,0;3.14159rad)
  sketch-geometry (6):
    g0: LineSegment StartX=-52 StartY=120.048 StartZ=0 EndX=-52 EndY=95.0481 EndZ=0
    g1: LineSegment StartX=-52 StartY=95.0481 StartZ=0 EndX=52 EndY=95.0481 EndZ=0
    g2: LineSegment StartX=52 StartY=95.0481 StartZ=0 EndX=52 EndY=120.048 EndZ=0
    g3: LineSegment StartX=52 StartY=120.048 StartZ=0 EndX=-52 EndY=120.048 EndZ=0
    g4: GeomPoint X=1e-16 Y=120.048 Z=0
    g5: GeomPoint X=0 Y=105.469 Z=0
  constraints (13):
    c: Coincident(g0,g1)
    c: Coincident(g1,g2)
    c: Coincident(g2,g3)
    c: Coincident(g3,g0)
    c: Vertical(g0)
    c: Vertical(g2)
    c: Horizontal(g3)
    c: PointOnObject(g5,g-2)
    c: Symmetric(g0,g2,g4)
    c: Symmetric(g1,g0,g-2)
    c: DistanceY(g0,g0) = 25
    c: DistanceX(g3,g3) = 104
    c: Block(g3)
FEATURE [PartDesign::Pad] Pad027
  BaseFeature = -> Pocket011
  Direction = (0,0,-1)
  Length = 2.2
  Length2 = 10
  Profile = -> Sketch043
  ReferenceAxis = -> Sketch043 [N_Axis]
  Refine = true
  Suppressed = false
  Type = 0
  expr: Length = <<dimensies002>>.DIKTE_FRONT
FEATURE [Sketcher::SketchObject] Sketch044
  ArcFitTolerance = 1e-06
  AttachmentSupport = -> [Pad027]
  FullyConstrained = true
  MakeInternals = false
  MapMode = 5
  sketch-geometry (5):
    g0: LineSegment StartX=-54.9901 StartY=-93.3363 StartZ=0 EndX=55.5099 EndY=-93.3363 EndZ=0
    g1: LineSegment StartX=-54.9901 StartY=-121.906 StartZ=0 EndX=55.5099 EndY=-121.906 EndZ=0
    g2: ArcOfCircle CenterX=-42.9824 CenterY=-107.621 CenterZ=0 NormalX=0 NormalY=0 NormalZ=1 AngleXU=0 Radius=18.6613 StartAngle=2.26979 EndAngle=4.01339
    g3: ArcOfCircle CenterX=42.9824 CenterY=-107.621 CenterZ=0 NormalX=0 NormalY=0 NormalZ=1 AngleXU=0 Radius=19 StartAngle=5.43233 EndAngle=7.13404
    g4: GeomPoint X=0 Y=-107.621 Z=0
  constraints (14):
    c: Horizontal(g0)
    c: Horizontal(g1)
    c: Coincident(g2,g0)
    c: Coincident(g2,g1)
    c: Coincident(g3,g0)
    c: Coincident(g3,g1)
    c: DistanceY(g1,g2) = 28.57
    c: DistanceX(g0,g0) = 110.5
    c: Horizontal(g3,g2)
    c: PointOnObject(g4,g-2)
    c: Symmetric(g2,g3,g4)
    c: Radius(g3) = 19
    c: Vertical(g1,g0)
    c: Block(g0)
FEATURE [PartDesign::Pad] Pad028
  BaseFeature = -> Pad027
  Direction = (0,0,1)
  Length = 8
  Length2 = 10
  Profile = -> Sketch044
  ReferenceAxis = -> Sketch044 [N_Axis]
  Refine = true
  Suppressed = false
  Type = 0
FEATURE [Sketcher::SketchObject] Sketch045
  ArcFitTolerance = 1e-06
  AttachmentSupport = -> [Pad028]
  ExternalGeometry = -> [Pad028]
  FullyConstrained = true
  MakeInternals = false
  MapMode = 5
  Placement = pos=(0,0,-67.8) rot=(1,0,0;3.14159rad)
  sketch-geometry (4):
    g0: LineSegment StartX=-9.32903 StartY=-91.8043 StartZ=0 EndX=9.40107 EndY=-91.8043 EndZ=0
    g1: LineSegment StartX=9.40107 StartY=-91.8043 StartZ=0 EndX=9.40107 EndY=-76.0875 EndZ=0
    g2: LineSegment StartX=9.40107 StartY=-76.0875 StartZ=0 EndX=-9.32903 EndY=-76.0875 EndZ=0
    g3: LineSegment StartX=-9.32903 StartY=-76.0875 StartZ=0 EndX=-9.32903 EndY=-91.8043 EndZ=0
  constraints (10):
    c: Coincident(g0,g1)
    c: Coincident(g1,g2)
    c: Coincident(g2,g3)
    c: Coincident(g3,g0)
    c: Horizontal(g0)
    c: Horizontal(g2)
    c: Vertical(g1)
    c: Vertical(g3)
    c: Coincident(g0,g-3)
    c: Coincident(g1,g-4)
FEATURE [PartDesign::Pad] Pad029
  BaseFeature = -> Pad028
  Direction = (0,0,-1)
  Length = 10
  Length2 = 10
  Profile = -> Sketch045
  ReferenceAxis = -> Sketch045 [N_Axis]
  Refine = true
  Reversed = true
  Suppressed = false
  Type = 3
  UpToFace = -> Pad028 [Face9]
FEATURE [PartDesign::Body] Body004
  AllowCompound = false
  Group = -> [Sketch035,Pad022,Sketch036,Pocket009,Sketch037,Pad023,Sketch038,Pad024,Sketch039,Pocket010,Sketch040,Pad025,Sketch041,Pad026,Sketch042,Pocket011,Sketch043,Pad027,Sketch044,Pad028,Sketch045,Pad029]
  Origin = -> Origin014
  Tip = -> Pad029
FEATURE [TechDraw::DrawProjGroupItem] ProjItem003  label="Left002"
  CoarseView = false
  Direction = (-1e-16,-1e-16,-1)
  Focus = 100
  HardHidden = false
  IsoCount = 0
  IsoHidden = false
  IsoVisible = false
  LockPosition = false
  Perspective = false
  Rotation = 0
  RotationVector = (1,0,0)
  ScaleType = 0
  ScrubCount = 1
  SeamHidden = false
  SeamVisible = false
  SmoothHidden = false
  SmoothVisible = true
  Source = -> [Body004]
  Type = 1
  X = 207.14
  XDirection = (0,-1,1e-16)
  Y = 0
FEATURE [Spreadsheet::Sheet] Spreadsheet002  label="dimensies002"
  cells = A3='dikte front; B3(DIKTE_FRONT)=2.2; C3='mm; A4='diepte; B4(DIEPTE)=70
FEATURE [TechDraw::DrawSVGTemplate] Template001
  Height = 297
  Orientation = 1
  Template = <path>
  Width = 420
FEATURE [Sketcher::SketchObject] Sketch046  label="bracing_master"
  ArcFitTolerance = 1e-06
  AttachmentSupport = -> [Pad009]
  ExternalGeometry = -> [Pad009]
  FullyConstrained = false
  MakeInternals = false
  MapMode = 5
  Placement = pos=(0,0,-2.2) rot=(1,0,0;3.14159rad)
  sketch-geometry (29):
    g0: LineSegment StartX=-75.375 StartY=-41.175 StartZ=0 EndX=75.375 EndY=-41.175 EndZ=0
    g1: LineSegment [constr] StartX=-4.8e-15 StartY=41.275 StartZ=0 EndX=-4.8e-15 EndY=-41.175 EndZ=0
    g2: LineSegment StartX=-75.375 StartY=-41.175 StartZ=0 EndX=-75.375 EndY=-47.525 EndZ=0
    g3: LineSegment StartX=-75.375 StartY=-47.525 StartZ=0 EndX=75.375 EndY=-47.525 EndZ=0
    g4: LineSegment StartX=75.375 StartY=-47.525 StartZ=0 EndX=75.375 EndY=-41.175 EndZ=0
    g5: LineSegment StartX=-1.6 StartY=187.625 StartZ=0 EndX=-1.6 EndY=47.625 EndZ=0
    g6: LineSegment StartX=-1.6 StartY=47.625 StartZ=0 EndX=1.6 EndY=47.625 EndZ=0
    g7: LineSegment StartX=1.6 StartY=47.625 StartZ=0 EndX=1.6 EndY=187.625 EndZ=0
    g8: LineSegment StartX=1.6 StartY=187.625 StartZ=0 EndX=-1.6 EndY=187.625 EndZ=0
    g9: GeomPoint X=-5.4e-15 Y=47.625 Z=0
    g10: LineSegment StartX=-30.75 StartY=41.275 StartZ=0 EndX=-42.75 EndY=-41.175 EndZ=0
    g11: LineSegment StartX=-47.8027 StartY=-41.175 StartZ=0 EndX=-35.8027 EndY=41.275 EndZ=0
    g12: LineSegment StartX=-35.8027 StartY=41.275 StartZ=0 EndX=-30.75 EndY=41.275 EndZ=0
    g13: LineSegment StartX=-47.8027 StartY=-41.175 StartZ=0 EndX=-42.75 EndY=-41.175 EndZ=0
    g14: LineSegment StartX=30.75 StartY=41.275 StartZ=0 EndX=42.75 EndY=-41.175 EndZ=0
    g15: LineSegment StartX=42.75 StartY=-41.175 StartZ=0 EndX=47.8027 EndY=-41.175 EndZ=0
    g16: LineSegment StartX=47.8027 StartY=-41.175 StartZ=0 EndX=35.8027 EndY=41.275 EndZ=0
    g17: LineSegment StartX=35.8027 StartY=41.275 StartZ=0 EndX=30.75 EndY=41.275 EndZ=0
    g18: LineSegment StartX=-32.6 StartY=47.625 StartZ=0 EndX=-65.0942 EndY=184.83 EndZ=0
    g19: LineSegment StartX=-65.0942 StartY=184.83 StartZ=0 EndX=-68.5 EndY=184.023 EndZ=0
    g20: LineSegment StartX=-68.5 StartY=184.023 StartZ=0 EndX=-36.1968 EndY=47.625 EndZ=0
    g21: LineSegment StartX=-36.1968 StartY=47.625 StartZ=0 EndX=-32.6 EndY=47.625 EndZ=0
    g22: LineSegment StartX=36.1968 StartY=47.625 StartZ=0 EndX=68.5 EndY=184.023 EndZ=0
    g23: LineSegment StartX=68.5 StartY=184.023 StartZ=0 EndX=65.0942 EndY=184.83 EndZ=0
    g24: LineSegment StartX=65.0942 StartY=184.83 StartZ=0 EndX=32.6 EndY=47.625 EndZ=0
    g25: LineSegment StartX=32.6 StartY=47.625 StartZ=0 EndX=36.1968 EndY=47.625 EndZ=0
    g26: LineSegment [constr] StartX=-68.5 StartY=184.023 StartZ=0 EndX=68.5 EndY=184.023 EndZ=0
    g27: GeomPoint [constr] X=0 Y=184.023 Z=0
    g28: LineSegment [constr] StartX=-35.0311 StartY=11.8606 StartZ=0 EndX=-39.9789 EndY=12.5807 EndZ=0
  constraints (75):
    c: Horizontal(g0)
    c: Symmetric(g-3,g-3,g1)
    c: Symmetric(g0,g0,g1)
    c: Vertical(g1)
    c: Coincident(g2,g0)
    c: Vertical(g2)
    c: Coincident(g3,g2)
    c: Horizontal(g3)
    c: Coincident(g4,g3)
    c: Coincident(g4,g0)
    c: Vertical(g4)
    c: Equal(g2,g-4)
    c: DistanceY(g1,g1) = 82.45
    c: DistanceX(g0,g0) = 150.75
    c: Coincident(g5,g6)
    c: Coincident(g6,g7)
    c: Coincident(g7,g8)
    c: Coincident(g8,g5)
    c: Vertical(g5)
    c: Vertical(g7)
    c: Horizontal(g6)
    c: Horizontal(g8)
    c: Symmetric(g6,g6,g9)
    c: Symmetric(g-4,g-5,g9)
    c: DistanceX(g8,g8) = 3.2
    c: DistanceY(g5,g5) = 140
    c: PointOnObject(g10,g-3)
    c: PointOnObject(g10,g0)
    c: PointOnObject(g11,g0)
    c: PointOnObject(g11,g-3)
    c: Coincident(g12,g11)
    c: Coincident(g12,g10)
    c: Coincident(g13,g11)
    c: Coincident(g13,g10)
    c: Coincident(g15,g14)
    c: Coincident(g16,g15)
    c: PointOnObject(g16,g-3)
    c: Coincident(g17,g16)
    c: Coincident(g17,g14)
    c: PointOnObject(g18,g-6)
    c: Coincident(g19,g18)
    c: Coincident(g20,g19)
    c: PointOnObject(g20,g-6)
    c: Coincident(g21,g20)
    c: Coincident(g21,g18)
    c: Coincident(g23,g22)
    c: Coincident(g24,g23)
    c: Coincident(g25,g24)
    c: Coincident(g25,g22)
    c: Symmetric(g18,g24,g9)
    c: Symmetric(g20,g22,g9)
    c: Coincident(g26,g19)
    c: Coincident(g26,g22)
    c: Horizontal(g26)
    c: Symmetric(g26,g26,g27)
    c: PointOnObject(g27,g-2)
    c: Perpendicular(g19,g18)
    c: Perpendicular(g23,g22)
    c: Equal(g19,g23)
    c: Parallel(g18,g20)
    c: DistanceX(g18,g5) = 31
    c: Distance(g19,g19) = 3.5
    c: DistanceX(g26,g26) = 137
    c: Distance(g18,g18) = 141
    c: Parallel(g11,g10)
    c: Parallel(g14,g16)
    c: DistanceX(g10,g14) = 61.5
    c: DistanceX(g10,g14) = 85.5
    c: Symmetric(g10,g14,g1)
    c: Symmetric(g10,g14,g1)
    c: Symmetric(g11,g15,g1)
    c: PointOnObject(g28,g10)
    c: PointOnObject(g28,g11)
    c: Perpendicular(g28,g10)
    c: Distance(g28) = 5
FEATURE [Sketcher::SketchObject] Sketch047
  ArcFitTolerance = 1e-06
  AttachmentSupport = -> [Pad009]
  ExternalGeometry = -> [Sketch046]
  FullyConstrained = true
  MakeInternals = false
  MapMode = 5
  Placement = pos=(0,0,-2.2) rot=(1,0,0;3.14159rad)
  sketch-geometry (4):
    g0: LineSegment StartX=-75.375 StartY=-41.175 StartZ=0 EndX=-75.375 EndY=-47.525 EndZ=0
    g1: LineSegment StartX=-75.375 StartY=-47.525 StartZ=0 EndX=75.375 EndY=-47.525 EndZ=0
    g2: LineSegment StartX=75.375 StartY=-47.525 StartZ=0 EndX=75.375 EndY=-41.175 EndZ=0
    g3: LineSegment StartX=75.375 StartY=-41.175 StartZ=0 EndX=-75.375 EndY=-41.175 EndZ=0
  constraints (8):
    c: Coincident(g-4,g0)
    c: Coincident(g0,g-5)
    c: Coincident(g0,g1)
    c: Coincident(g1,g-6)
    c: Coincident(g1,g2)
    c: Coincident(g2,g-6)
    c: Coincident(g2,g3)
    c: Coincident(g3,g0)
FEATURE [PartDesign::Pad] Pad030
  BaseFeature = -> Pad009
  Direction = (0,0,-1)
  Length = 8
  Length2 = 10
  Profile = -> Sketch047
  ReferenceAxis = -> Sketch047 [N_Axis]
  Refine = true
  Suppressed = false
  Type = 0
FEATURE [Sketcher::SketchObject] Sketch048
  ArcFitTolerance = 1e-06
  AttachmentSupport = -> [Pad030]
  ExternalGeometry = -> [Sketch046]
  FullyConstrained = true
  MakeInternals = false
  MapMode = 5
  Placement = pos=(0,0,-2.2) rot=(1,0,0;3.14159rad)
  sketch-geometry (8):
    g0: LineSegment StartX=-35.8027 StartY=41.275 StartZ=0 EndX=-30.75 EndY=41.275 EndZ=0
    g1: LineSegment StartX=-30.75 StartY=41.275 StartZ=0 EndX=-42.75 EndY=-41.175 EndZ=0
    g2: LineSegment StartX=-42.75 StartY=-41.175 StartZ=0 EndX=-47.8027 EndY=-41.175 EndZ=0
    g3: LineSegment StartX=-47.8027 StartY=-41.175 StartZ=0 EndX=-35.8027 EndY=41.275 EndZ=0
    g4: LineSegment StartX=30.75 StartY=41.275 StartZ=0 EndX=35.8027 EndY=41.275 EndZ=0
    g5: LineSegment StartX=35.8027 StartY=41.275 StartZ=0 EndX=47.8027 EndY=-41.175 EndZ=0
    g6: LineSegment StartX=47.8027 StartY=-41.175 StartZ=0 EndX=42.75 EndY=-41.175 EndZ=0
    g7: LineSegment StartX=42.75 StartY=-41.175 StartZ=0 EndX=30.75 EndY=41.275 EndZ=0
  constraints (16):
    c: Coincident(g-3,g0)
    c: Coincident(g0,g-4)
    c: Coincident(g0,g1)
    c: Coincident(g1,g-4)
    c: Coincident(g1,g2)
    c: Coincident(g2,g-3)
    c: Coincident(g2,g3)
    c: Coincident(g3,g0)
    c: Coincident(g-5,g4)
    c: Coincident(g4,g-6)
    c: Coincident(g4,g5)
    c: Coincident(g5,g-6)
    c: Coincident(g5,g6)
    c: Coincident(g6,g-5)
    c: Coincident(g6,g7)
    c: Coincident(g7,g4)
FEATURE [PartDesign::Pad] Pad031
  BaseFeature = -> Pad030
  Direction = (0,0,-1)
  Length = 2
  Length2 = 10
  Profile = -> Sketch048
  ReferenceAxis = -> Sketch048 [N_Axis]
  Refine = true
  Suppressed = false
  Type = 0
FEATURE [Sketcher::SketchObject] Sketch049
  ArcFitTolerance = 1e-06
  AttachmentSupport = -> [Pad031]
  ExternalGeometry = -> [Sketch046]
  FullyConstrained = true
  MakeInternals = false
  MapMode = 5
  Placement = pos=(0,0,-2.2) rot=(1,0,0;3.14159rad)
  sketch-geometry (12):
    g0: LineSegment StartX=-68.5 StartY=184.023 StartZ=0 EndX=-65.0942 EndY=184.83 EndZ=0
    g1: LineSegment StartX=-65.0942 StartY=184.83 StartZ=0 EndX=-32.6 EndY=47.625 EndZ=0
    g2: LineSegment StartX=-32.6 StartY=47.625 StartZ=0 EndX=-36.1968 EndY=47.625 EndZ=0
    g3: LineSegment StartX=-36.1968 StartY=47.625 StartZ=0 EndX=-68.5 EndY=184.023 EndZ=0
    g4: LineSegment StartX=-1.6 StartY=187.625 StartZ=0 EndX=1.6 EndY=187.625 EndZ=0
    g5: LineSegment StartX=1.6 StartY=187.625 StartZ=0 EndX=1.6 EndY=47.625 EndZ=0
    g6: LineSegment StartX=1.6 StartY=47.625 StartZ=0 EndX=-1.6 EndY=47.625 EndZ=0
    g7: LineSegment StartX=-1.6 StartY=47.625 StartZ=0 EndX=-1.6 EndY=187.625 EndZ=0
    g8: LineSegment StartX=65.0942 StartY=184.83 StartZ=0 EndX=68.5 EndY=184.023 EndZ=0
    g9: LineSegment StartX=68.5 StartY=184.023 StartZ=0 EndX=36.1968 EndY=47.625 EndZ=0
    g10: LineSegment StartX=36.1968 StartY=47.625 StartZ=0 EndX=32.6 EndY=47.625 EndZ=0
    g11: LineSegment StartX=32.6 StartY=47.625 StartZ=0 EndX=65.0942 EndY=184.83 EndZ=0
  constraints (24):
    c: Coincident(g-3,g0)
    c: Coincident(g0,g-4)
    c: Coincident(g0,g1)
    c: Coincident(g1,g-4)
    c: Coincident(g1,g2)
    c: Coincident(g2,g-3)
    c: Coincident(g2,g3)
    c: Coincident(g3,g0)
    c: Coincident(g-5,g4)
    c: Coincident(g4,g-6)
    c: Coincident(g4,g5)
    c: Coincident(g5,g-6)
    c: Coincident(g5,g6)
    c: Coincident(g6,g-5)
    c: Coincident(g6,g7)
    c: Coincident(g7,g4)
    c: Coincident(g-7,g8)
    c: Coincident(g8,g-8)
    c: Coincident(g8,g9)
    c: Coincident(g9,g-8)
    c: Coincident(g9,g10)
    c: Coincident(g10,g-7)
    c: Coincident(g10,g11)
    c: Coincident(g11,g8)
FEATURE [PartDesign::Pad] Pad032
  BaseFeature = -> Pad031
  Direction = (0,0,-1)
  Length = 5.5
  Length2 = 10
  Profile = -> Sketch049
  ReferenceAxis = -> Sketch049 [N_Axis]
  Refine = true
  Suppressed = false
  Type = 0
FEATURE [Sketcher::SketchObject] Sketch050
  ArcFitTolerance = 1e-06
  AttachmentSupport = -> [Pad032]
  ExternalGeometry = -> [Pad032]
  FullyConstrained = true
  MakeInternals = false
  MapMode = 5
  Placement = pos=(0,0,-67.8) rot=(1,0,0;3.14159rad)
  sketch-geometry (12):
    g0: LineSegment StartX=-65 StartY=20.6875 StartZ=0 EndX=-65 EndY=14.3375 EndZ=0
    g1: LineSegment StartX=-65 StartY=14.3375 StartZ=0 EndX=65 EndY=14.3375 EndZ=0
    g2: LineSegment StartX=65 StartY=14.3375 StartZ=0 EndX=65 EndY=20.6875 EndZ=0
    g3: LineSegment StartX=65 StartY=20.6875 StartZ=0 EndX=-65 EndY=20.6875 EndZ=0
    g4: LineSegment StartX=-113 StartY=119.087 StartZ=0 EndX=-113 EndY=112.737 EndZ=0
    g5: LineSegment StartX=-113 StartY=112.737 StartZ=0 EndX=113 EndY=112.737 EndZ=0
    g6: LineSegment StartX=113 StartY=112.737 StartZ=0 EndX=113 EndY=119.087 EndZ=0
    g7: LineSegment StartX=113 StartY=119.087 StartZ=0 EndX=-113 EndY=119.087 EndZ=0
    g8: GeomPoint X=-65 Y=17.5125 Z=0
    g9: GeomPoint X=0 Y=20.6875 Z=0
    g10: GeomPoint X=0 Y=119.087 Z=0
    g11: GeomPoint X=-113 Y=115.912 Z=0
  constraints (28):
    c: Coincident(g0,g1)
    c: Coincident(g1,g2)
    c: Coincident(g2,g3)
    c: Coincident(g3,g0)
    c: Vertical(g0)
    c: Vertical(g2)
    c: Horizontal(g1)
    c: Horizontal(g3)
    c: Coincident(g4,g5)
    c: Coincident(g5,g6)
    c: Coincident(g6,g7)
    c: Coincident(g7,g4)
    c: Vertical(g4)
    c: Vertical(g6)
    c: Horizontal(g5)
    c: Horizontal(g7)
    c: Equal(g2,g-6)
    c: Equal(g6,g2)
    c: Symmetric(g0,g0,g8)
    c: Symmetric(g3,g3,g9)
    c: PointOnObject(g9,g-2)
    c: Symmetric(g7,g7,g10)
    c: Symmetric(g4,g4,g11)
    c: PointOnObject(g10,g-2)
    c: DistanceY(g-3,g8) = 111.1
    c: DistanceX(g1,g1) = 130
    c: DistanceY(g-3,g11) = 209.5
    c: DistanceX(g5,g5) = 226
FEATURE [PartDesign::Pad] Pad033
  BaseFeature = -> Pad032
  Direction = (0,0,-1)
  Length = 8
  Length2 = 10
  Profile = -> Sketch050
  ReferenceAxis = -> Sketch050 [N_Axis]
  Refine = true
  Reversed = true
  Suppressed = false
  Type = 0
FEATURE [PartDesign::Body] Body001  label="Body"
  AllowCompound = false
  Group = -> [Sketch003,Pad,Sketch004,Pocket,Sketch005,Pad001,Sketch006,Pad002,Sketch007,Pocket001,Sketch008,Pad003,Sketch009,Pad004,Sketch010,Pocket002,Sketch011,Pad005,Sketch012,Pad006,Sketch015,Pad009,Sketch046,Sketch047,Pad030,Sketch048,Pad031,Sketch049,Pad032,Sketch050,Pad033]
  Origin = -> Origin001
  Tip = -> Pad033
FEATURE [App::Part] Part  label="kast"
  Group = -> [Body001]
  Origin = -> Origin002
FEATURE [TechDraw::DrawProjGroupItem] View  label="Front"
  CoarseView = false
  Direction = (0,-1,0)
  Focus = 100
  HardHidden = false
  IsoCount = 0
  IsoHidden = false
  IsoVisible = false
  LockPosition = true
  Perspective = false
  Rotation = 0
  RotationVector = (1,0,0)
  ScaleType = 2
  ScrubCount = 1
  SeamHidden = false
  SeamVisible = false
  SmoothHidden = false
  SmoothVisible = true
  Source = -> [Body001]
  Type = 0
  X = 0
  XDirection = (1e-16,0,1)
  Y = 0
FEATURE [TechDraw::DrawProjGroupItem] ProjItem001  label="Left"
  CoarseView = false
  Direction = (-1e-16,-1e-16,-1)
  Focus = 100
  HardHidden = false
  IsoCount = 0
  IsoHidden = false
  IsoVisible = false
  LockPosition = false
  Perspective = false
  Rotation = 0
  RotationVector = (1,0,0)
  ScaleType = 0
  ScrubCount = 1
  SeamHidden = false
  SeamVisible = false
  SmoothHidden = false
  SmoothVisible = true
  Source = -> [Body001]
  Type = 1
  X = 206.257
  XDirection = (0,-1,1e-16)
  Y = 0
FEATURE [TechDraw::DrawProjGroup] ProjGroup
  Anchor = -> View
  AutoDistribute = true
  LockPosition = false
  ProjectionType = 0
  Rotation = 0
  ScaleType = 0
  Source = -> [Body001]
  Views = -> [View,ProjItem001]
  X = 146.886
  Y = 215.267
  spacingX = 15
  spacingY = 15
FEATURE [TechDraw::DrawViewDimension] Dimension
  AngleOverride = false
  Arbitrary = false
  ArbitraryTolerances = false
  BoxCorners = (2) [(-152.257,-114.765,-1e-07),(152.257,114.765,1e-07)]
  EqualTolerance = true
  ExtensionAngle = 0
  FormatSpec = %.2w
  FormatSpecOverTolerance = %+.2w
  FormatSpecUnderTolerance = %+.2w
  Inverted = false
  LineAngle = 0
  LockPosition = false
  MeasureType = 1
  OverTolerance = 0
  References2D = -> [ProjItem001]
  Rotation = 0
  ScaleType = 0
  TheoreticalExact = false
  Type = 1
  UnderTolerance = 0
  X = -4.51223
  Y = 128.336
FEATURE [TechDraw::DrawViewDimension] Dimension002
  AngleOverride = false
  Arbitrary = false
  ArbitraryTolerances = false
  BoxCorners = (2) [(-39,-114.765,-1e-07),(39,114.765,1e-07)]
  EqualTolerance = true
  ExtensionAngle = 0
  FormatSpec = %.2w
  FormatSpecOverTolerance = %+.2w
  FormatSpecUnderTolerance = %+.2w
  Inverted = false
  LineAngle = 0
  LockPosition = false
  MeasureType = 1
  OverTolerance = 0
  References2D = -> [View]
  Rotation = 0
  ScaleType = 0
  TheoreticalExact = false
  Type = 2
  UnderTolerance = 0
  X = -63.8905
  Y = 69.9022
FEATURE [TechDraw::DrawViewDimension] Dimension003
  AngleOverride = false
  Arbitrary = false
  ArbitraryTolerances = false
  BoxCorners = (2) [(-152.257,-114.765,-1e-07),(152.257,114.765,1e-07)]
  EqualTolerance = true
  ExtensionAngle = 0
  FormatSpec = %.2w
  FormatSpecOverTolerance = %+.2w
  FormatSpecUnderTolerance = %+.2w
  Inverted = false
  LineAngle = 0
  LockPosition = false
  MeasureType = 1
  OverTolerance = 0
  References2D = -> [ProjItem001]
  Rotation = 0
  ScaleType = 0
  TheoreticalExact = false
  Type = 8
  UnderTolerance = 0
  X = -44.162
  Y = 42.2781
FEATURE [TechDraw::DrawViewDimension] Dimension004
  AngleOverride = false
  Arbitrary = false
  ArbitraryTolerances = false
  BoxCorners = (2) [(-152.257,-114.765,-1e-07),(152.257,114.765,1e-07)]
  EqualTolerance = true
  ExtensionAngle = 0
  FormatSpec = %.2w
  FormatSpecOverTolerance = %+.2w
  FormatSpecUnderTolerance = %+.2w
  Inverted = false
  LineAngle = 0
  LockPosition = false
  MeasureType = 1
  OverTolerance = 0
  References2D = -> [ProjItem001]
  Rotation = 0
  ScaleType = 0
  TheoreticalExact = false
  Type = 0
  UnderTolerance = 0
  X = -38.2059
  Y = -42.934
FEATURE [TechDraw::DrawViewDimension] Dimension005
  AngleOverride = false
  Arbitrary = false
  ArbitraryTolerances = false
  BoxCorners = (2) [(-152.257,-114.765,-1e-07),(152.257,114.765,1e-07)]
  EqualTolerance = true
  ExtensionAngle = 0
  FormatSpec = %.2w
  FormatSpecOverTolerance = %+.2w
  FormatSpecUnderTolerance = %+.2w
  Inverted = false
  LineAngle = 0
  LockPosition = false
  MeasureType = 1
  OverTolerance = 0
  References2D = -> [ProjItem001]
  Rotation = 0
  ScaleType = 0
  TheoreticalExact = false
  Type = 0
  UnderTolerance = 0
  X = -112.359
  Y = -108.598
FEATURE [TechDraw::DrawViewDimension] Dimension006
  AngleOverride = false
  Arbitrary = false
  ArbitraryTolerances = false
  BoxCorners = (2) [(-152.257,-114.765,-1e-07),(152.257,114.765,1e-07)]
  EqualTolerance = true
  ExtensionAngle = 0
  FormatSpec = %.2w
  FormatSpecOverTolerance = %+.2w
  FormatSpecUnderTolerance = %+.2w
  Inverted = false
  LineAngle = 0
  LockPosition = false
  MeasureType = 1
  OverTolerance = 0
  References2D = -> [ProjItem001]
  Rotation = 0
  ScaleType = 0
  TheoreticalExact = false
  Type = 1
  UnderTolerance = 0
  X = 36.5059
  Y = 104.492
FEATURE [TechDraw::DrawViewDimension] Dimension007
  AngleOverride = false
  Arbitrary = false
  ArbitraryTolerances = false
  BoxCorners = (2) [(-152.257,-114.765,-1e-07),(152.257,114.765,1e-07)]
  EqualTolerance = true
  ExtensionAngle = 0
  FormatSpec = %.2w
  FormatSpecOverTolerance = %+.2w
  FormatSpecUnderTolerance = %+.2w
  Inverted = false
  LineAngle = 0
  LockPosition = false
  MeasureType = 1
  OverTolerance = 0
  References2D = -> [ProjItem001]
  Rotation = 0
  ScaleType = 0
  TheoreticalExact = false
  Type = 1
  UnderTolerance = 0
  X = 8.85631
  Y = 77.7109
FEATURE [TechDraw::DrawViewDimension] Dimension008
  AngleOverride = false
  Arbitrary = false
  ArbitraryTolerances = false
  BoxCorners = (2) [(-152.257,-114.765,-1e-07),(152.257,114.765,1e-07)]
  EqualTolerance = true
  ExtensionAngle = 0
  FormatSpec = %.2w
  FormatSpecOverTolerance = %+.2w
  FormatSpecUnderTolerance = %+.2w
  Inverted = false
  LineAngle = 0
  LockPosition = false
  MeasureType = 1
  OverTolerance = 0
  References2D = -> [ProjItem001]
  Rotation = 0
  ScaleType = 0
  TheoreticalExact = false
  Type = 1
  UnderTolerance = 0
  X = 45.4489
  Y = 70.7109
FEATURE [TechDraw::DrawViewDimension] Dimension009
  AngleOverride = false
  Arbitrary = false
  ArbitraryTolerances = false
  BoxCorners = (2) [(-152.257,-114.765,-1e-07),(152.257,114.765,1e-07)]
  EqualTolerance = true
  ExtensionAngle = 0
  FormatSpec = %.2w
  FormatSpecOverTolerance = %+.2w
  FormatSpecUnderTolerance = %+.2w
  Inverted = false
  LineAngle = 0
  LockPosition = false
  MeasureType = 1
  OverTolerance = 0
  References2D = -> [ProjItem001]
  Rotation = 0
  ScaleType = 0
  TheoreticalExact = false
  Type = 1
  UnderTolerance = 0
  X = -29.0802
  Y = 89.9068
FEATURE [TechDraw::DrawViewDimension] Dimension010
  AngleOverride = false
  Arbitrary = false
  ArbitraryTolerances = false
  BoxCorners = (2) [(-152.257,-114.765,-1e-07),(152.257,114.765,1e-07)]
  EqualTolerance = true
  ExtensionAngle = 0
  FormatSpec = %.2w
  FormatSpecOverTolerance = %+.2w
  FormatSpecUnderTolerance = %+.2w
  Inverted = false
  LineAngle = 0
  LockPosition = false
  MeasureType = 1
  OverTolerance = 0
  References2D = -> [ProjItem001]
  Rotation = 0
  ScaleType = 0
  TheoreticalExact = false
  Type = 1
  UnderTolerance = 0
  X = -103.147
  Y = 38.5013
FEATURE [TechDraw::DrawViewDimension] Dimension011
  AngleOverride = false
  Arbitrary = false
  ArbitraryTolerances = false
  BoxCorners = (2) [(-152.257,-114.765,-1e-07),(152.257,114.765,1e-07)]
  EqualTolerance = true
  ExtensionAngle = 0
  FormatSpec = %.2w
  FormatSpecOverTolerance = %+.2w
  FormatSpecUnderTolerance = %+.2w
  Inverted = false
  LineAngle = 0
  LockPosition = false
  MeasureType = 1
  OverTolerance = 0
  References2D = -> [ProjItem001]
  Rotation = 0
  ScaleType = 0
  TheoreticalExact = false
  Type = 2
  UnderTolerance = 0
  X = -115.021
  Y = -43.4377
FEATURE [TechDraw::DrawPage] Page  label="A2_drawing"
  KeepUpdated = true
  NextBalloonIndex = 1
  ProjectionType = 0
  Template = -> Template
  Views = -> [ProjGroup,Dimension,Dimension002,Dimension003,Dimension004,Dimension005,Dimension006,Dimension007,Dimension008,Dimension009,Dimension010,Dimension011]
FEATURE [TechDraw::DrawHatch] Hatch
  HatchPattern = <path>
  Source = -> ProjItem001 [Face6]
FEATURE [TechDraw::DrawHatch] Hatch001
  HatchPattern = <path>
  Source = -> ProjItem001 [Face8]
FEATURE [TechDraw::DrawProjGroupItem] View001  label="Vooraanzicht"
  CoarseView = false
  Direction = (0,0,-1)
  Focus = 3
  HardHidden = true
  IsoCount = 0
  IsoHidden = true
  IsoVisible = false
  LockPosition = false
  Perspective = false
  Rotation = 0
  RotationVector = (1,0,0)
  ScaleType = 0
  ScrubCount = 1
  SeamHidden = true
  SeamVisible = false
  SmoothHidden = true
  SmoothVisible = true
  Source = -> [Part]
  Type = 0
  X = 210.157
  XDirection = (1e-16,-1,0)
  Y = 148.709
FEATURE [TechDraw::DrawViewDimExtent] DimExtent
  AngleOverride = false
  Arbitrary = false
  ArbitraryTolerances = false
  BoxCorners = (2) [(-152.257,-114.765,-1e-07),(152.257,114.765,1e-07)]
  DirExtent = 0
  EqualTolerance = true
  ExtensionAngle = 0
  FormatSpec = %.2w
  FormatSpecOverTolerance = %+.2w
  FormatSpecUnderTolerance = %+.2w
  Inverted = false
  LineAngle = 0
  LockPosition = false
  MeasureType = 1
  OverTolerance = 0
  References2D = -> [View001]
  Rotation = 0
  ScaleType = 0
  Source = -> [View001]
  TheoreticalExact = false
  Type = 1
  UnderTolerance = 0
  X = -2.87419
  Y = 133.171
FEATURE [TechDraw::DrawViewDimExtent] DimExtent001
  AngleOverride = false
  Arbitrary = false
  ArbitraryTolerances = false
  BoxCorners = (2) [(-152.257,-114.765,-1e-07),(152.257,114.765,1e-07)]
  DirExtent = 1
  EqualTolerance = true
  ExtensionAngle = 0
  FormatSpec = %.2w
  FormatSpecOverTolerance = %+.2w
  FormatSpecUnderTolerance = %+.2w
  Inverted = false
  LineAngle = 0
  LockPosition = false
  MeasureType = 1
  OverTolerance = 0
  References2D = -> [View001]
  Rotation = 0
  ScaleType = 0
  Source = -> [View001]
  TheoreticalExact = false
  Type = 2
  UnderTolerance = 0
  X = 165.795
  Y = 128.919
FEATURE [TechDraw::DrawViewDimension] Dimension012
  AngleOverride = false
  Arbitrary = false
  ArbitraryTolerances = false
  BoxCorners = (2) [(-152.257,-114.765,-1e-07),(152.257,114.765,1e-07)]
  EqualTolerance = true
  ExtensionAngle = 0
  FormatSpec = ⌀%.2w
  FormatSpecOverTolerance = %+.2w
  FormatSpecUnderTolerance = %+.2w
  Inverted = false
  LineAngle = 0
  LockPosition = false
  MeasureType = 1
  OverTolerance = 0
  References2D = -> [View001]
  Rotation = 0
  ScaleType = 0
  TheoreticalExact = false
  Type = 5
  UnderTolerance = 0
  X = -93.9851
  Y = 35.2324
FEATURE [TechDraw::DrawViewDimension] Dimension013
  AngleOverride = false
  Arbitrary = false
  ArbitraryTolerances = false
  BoxCorners = (2) [(-152.257,-114.765,-1e-07),(152.257,114.765,1e-07)]
  EqualTolerance = true
  ExtensionAngle = 0
  FormatSpec = %.2w
  FormatSpecOverTolerance = %+.2w
  FormatSpecUnderTolerance = %+.2w
  Inverted = false
  LineAngle = 0
  LockPosition = false
  MeasureType = 1
  OverTolerance = 0
  References2D = -> [View001]
  Rotation = 0
  ScaleType = 0
  TheoreticalExact = false
  Type = 1
  UnderTolerance = 0
  X = -105.464
  Y = -61.3331
FEATURE [TechDraw::DrawViewDimension] Dimension014
  AngleOverride = false
  Arbitrary = false
  ArbitraryTolerances = false
  BoxCorners = (2) [(-152.257,-114.765,-1e-07),(152.257,114.765,1e-07)]
  EqualTolerance = true
  ExtensionAngle = 0
  FormatSpec = %.2w
  FormatSpecOverTolerance = %+.2w
  FormatSpecUnderTolerance = %+.2w
  Inverted = false
  LineAngle = 0
  LockPosition = false
  MeasureType = 1
  OverTolerance = 0
  References2D = -> [View001]
  Rotation = 0
  ScaleType = 0
  TheoreticalExact = false
  Type = 1
  UnderTolerance = 0
  X = 43.8193
  Y = -78.0365
FEATURE [TechDraw::DrawHatch] Hatch002
  HatchPattern = <path>
  Source = -> View001 [Face6,Face5]
FEATURE [TechDraw::DrawViewDimension] Dimension015
  AngleOverride = false
  Arbitrary = false
  ArbitraryTolerances = false
  BoxCorners = (2) [(-152.257,-114.765,-1e-07),(152.257,114.765,1e-07)]
  EqualTolerance = true
  ExtensionAngle = 0
  FormatSpec = %.2w
  FormatSpecOverTolerance = %+.2w
  FormatSpecUnderTolerance = %+.2w
  Inverted = false
  LineAngle = 0
  LockPosition = false
  MeasureType = 1
  OverTolerance = 0
  References2D = -> [View001]
  Rotation = 0
  ScaleType = 0
  TheoreticalExact = false
  Type = 0
  UnderTolerance = 0
  X = -142.616
  Y = 20.8469
FEATURE [TechDraw::DrawViewDimension] Dimension016
  AngleOverride = false
  Arbitrary = false
  ArbitraryTolerances = false
  BoxCorners = (2) [(-152.257,-114.765,-1e-07),(152.257,114.765,1e-07)]
  EqualTolerance = true
  ExtensionAngle = 0
  FormatSpec = %.2w
  FormatSpecOverTolerance = %+.2w
  FormatSpecUnderTolerance = %+.2w
  Inverted = false
  LineAngle = 0
  LockPosition = false
  MeasureType = 1
  OverTolerance = 0
  References2D = -> [View001]
  Rotation = 0
  ScaleType = 0
  TheoreticalExact = false
  Type = 2
  UnderTolerance = 0
  X = -175.623
  Y = -0.03602
FEATURE [TechDraw::DrawViewDimension] Dimension017
  AngleOverride = false
  Arbitrary = false
  ArbitraryTolerances = false
  BoxCorners = (2) [(-152.257,-114.765,-1e-07),(152.257,114.765,1e-07)]
  EqualTolerance = true
  ExtensionAngle = 0
  FormatSpec = %.2w
  FormatSpecOverTolerance = %+.2w
  FormatSpecUnderTolerance = %+.2w
  Inverted = false
  LineAngle = 0
  LockPosition = false
  MeasureType = 1
  OverTolerance = 0
  References2D = -> [View001]
  Rotation = 0
  ScaleType = 0
  TheoreticalExact = false
  Type = 2
  UnderTolerance = 0
  X = -194.346
  Y = 0
FEATURE [TechDraw::DrawViewDimension] Dimension018
  AngleOverride = false
  Arbitrary = false
  ArbitraryTolerances = false
  BoxCorners = (2) [(-152.257,-114.765,-1e-07),(152.257,114.765,1e-07)]
  EqualTolerance = true
  ExtensionAngle = 0
  FormatSpec = %.2w
  FormatSpecOverTolerance = %+.2w
  FormatSpecUnderTolerance = %+.2w
  Inverted = false
  LineAngle = 0
  LockPosition = false
  MeasureType = 1
  OverTolerance = 0
  References2D = -> [View001]
  Rotation = 0
  ScaleType = 0
  TheoreticalExact = false
  Type = 1
  UnderTolerance = 0
  X = -135.535
  Y = 73.8062
FEATURE [TechDraw::DrawViewDimension] Dimension019
  AngleOverride = false
  Arbitrary = false
  ArbitraryTolerances = false
  BoxCorners = (2) [(-152.257,-114.765,-1e-07),(152.257,114.765,1e-07)]
  EqualTolerance = true
  ExtensionAngle = 0
  FormatSpec = %.2w
  FormatSpecOverTolerance = %+.2w
  FormatSpecUnderTolerance = %+.2w
  Inverted = false
  LineAngle = 0
  LockPosition = false
  MeasureType = 1
  OverTolerance = 0
  References2D = -> [View001]
  Rotation = 0
  ScaleType = 0
  TheoreticalExact = false
  Type = 1
  UnderTolerance = 0
  X = -136.426
  Y = 89.3725
FEATURE [TechDraw::DrawViewDimension] Dimension020
  AngleOverride = false
  Arbitrary = false
  ArbitraryTolerances = false
  BoxCorners = (2) [(-152.257,-114.765,-1e-07),(152.257,114.765,1e-07)]
  EqualTolerance = true
  ExtensionAngle = 0
  FormatSpec = %.2w
  FormatSpecOverTolerance = %+.2w
  FormatSpecUnderTolerance = %+.2w
  Inverted = false
  LineAngle = 0
  LockPosition = false
  MeasureType = 1
  OverTolerance = 0
  References2D = -> [View001]
  Rotation = 0
  ScaleType = 0
  TheoreticalExact = false
  Type = 1
  UnderTolerance = 0
  X = -38.0324
  Y = 105.903
FEATURE [TechDraw::DrawViewDimension] Dimension021
  AngleOverride = false
  Arbitrary = false
  ArbitraryTolerances = false
  BoxCorners = (2) [(-152.257,-114.765,-1e-07),(152.257,114.765,1e-07)]
  EqualTolerance = true
  ExtensionAngle = 0
  FormatSpec = %.2w
  FormatSpecOverTolerance = %+.2w
  FormatSpecUnderTolerance = %+.2w
  Inverted = false
  LineAngle = 0
  LockPosition = false
  MeasureType = 1
  OverTolerance = 0
  References2D = -> [View001]
  Rotation = 0
  ScaleType = 0
  TheoreticalExact = false
  Type = 1
  UnderTolerance = 0
  X = -9.82694
  Y = 98.9033
FEATURE [TechDraw::DrawViewDimension] Dimension022
  AngleOverride = false
  Arbitrary = false
  ArbitraryTolerances = false
  BoxCorners = (2) [(-152.257,-114.765,-1e-07),(152.257,114.765,1e-07)]
  EqualTolerance = true
  ExtensionAngle = 0
  FormatSpec = %.2w
  FormatSpecOverTolerance = %+.2w
  FormatSpecUnderTolerance = %+.2w
  Inverted = false
  LineAngle = 0
  LockPosition = false
  MeasureType = 1
  OverTolerance = 0
  References2D = -> [View001]
  Rotation = 0
  ScaleType = 0
  TheoreticalExact = false
  Type = 0
  UnderTolerance = 0
  X = 5.67695
  Y = 77.3393
FEATURE [TechDraw::DrawViewDimension] Dimension023
  AngleOverride = false
  Arbitrary = false
  ArbitraryTolerances = false
  BoxCorners = (2) [(-152.257,-114.765,-1e-07),(152.257,114.765,1e-07)]
  EqualTolerance = true
  ExtensionAngle = 0
  FormatSpec = %.2w
  FormatSpecOverTolerance = %+.2w
  FormatSpecUnderTolerance = %+.2w
  Inverted = false
  LineAngle = 0
  LockPosition = false
  MeasureType = 1
  OverTolerance = 0
  References2D = -> [View001]
  Rotation = 0
  ScaleType = 0
  TheoreticalExact = false
  Type = 1
  UnderTolerance = 0
  X = 64.2602
  Y = -68.3331
FEATURE [TechDraw::DrawViewDimension] Dimension024
  AngleOverride = false
  Arbitrary = false
  ArbitraryTolerances = false
  BoxCorners = (2) [(-152.257,-114.765,-1e-07),(152.257,114.765,1e-07)]
  EqualTolerance = true
  ExtensionAngle = 0
  FormatSpec = %.2w
  FormatSpecOverTolerance = %+.2w
  FormatSpecUnderTolerance = %+.2w
  Inverted = false
  LineAngle = 0
  LockPosition = false
  MeasureType = 1
  OverTolerance = 0
  References2D = -> [View001]
  Rotation = 0
  ScaleType = 0
  TheoreticalExact = false
  Type = 0
  UnderTolerance = 0
  X = 105.381
  Y = 4.74217
FEATURE [TechDraw::DrawViewDimension] Dimension025
  AngleOverride = false
  Arbitrary = false
  ArbitraryTolerances = false
  BoxCorners = (2) [(-152.257,-114.765,-1e-07),(152.257,114.765,1e-07)]
  EqualTolerance = true
  ExtensionAngle = 0
  FormatSpec = %.2w
  FormatSpecOverTolerance = %+.2w
  FormatSpecUnderTolerance = %+.2w
  Inverted = false
  LineAngle = 0
  LockPosition = false
  MeasureType = 1
  OverTolerance = 0
  References2D = -> [View001]
  Rotation = 0
  ScaleType = 0
  TheoreticalExact = false
  Type = 0
  UnderTolerance = 0
  X = 127.209
  Y = 35.6501
FEATURE [TechDraw::DrawViewDimension] Dimension026
  AngleOverride = false
  Arbitrary = false
  ArbitraryTolerances = false
  BoxCorners = (2) [(-152.257,-114.765,-1e-07),(152.257,114.765,1e-07)]
  EqualTolerance = true
  ExtensionAngle = 0
  FormatSpec = %.2w
  FormatSpecOverTolerance = %+.2w
  FormatSpecUnderTolerance = %+.2w
  Inverted = false
  LineAngle = 0
  LockPosition = false
  MeasureType = 1
  OverTolerance = 0
  References2D = -> [View001]
  Rotation = 0
  ScaleType = 0
  TheoreticalExact = false
  Type = 0
  UnderTolerance = 0
  X = 143.973
  Y = 0.092833
FEATURE [TechDraw::DrawViewDimension] Dimension027
  AngleOverride = false
  Arbitrary = false
  ArbitraryTolerances = false
  BoxCorners = (2) [(-152.257,-114.765,-1e-07),(152.257,114.765,1e-07)]
  EqualTolerance = true
  ExtensionAngle = 0
  FormatSpec = %.2w
  FormatSpecOverTolerance = %+.2w
  FormatSpecUnderTolerance = %+.2w
  Inverted = false
  LineAngle = 0
  LockPosition = false
  MeasureType = 1
  OverTolerance = 0
  References2D = -> [View001]
  Rotation = 0
  ScaleType = 0
  TheoreticalExact = false
  Type = 0
  UnderTolerance = 0
  X = 3.21114
  Y = 47.1706
FEATURE [TechDraw::DrawViewDimension] Dimension028
  AngleOverride = false
  Arbitrary = false
  ArbitraryTolerances = false
  BoxCorners = (2) [(-152.257,-114.765,-1e-07),(152.257,114.765,1e-07)]
  EqualTolerance = true
  ExtensionAngle = 0
  FormatSpec = %.2w
  FormatSpecOverTolerance = %+.2w
  FormatSpecUnderTolerance = %+.2w
  Inverted = false
  LineAngle = 0
  LockPosition = false
  MeasureType = 1
  OverTolerance = 0
  References2D = -> [View001]
  Rotation = 0
  ScaleType = 0
  TheoreticalExact = false
  Type = 0
  UnderTolerance = 0
  X = -82.2099
  Y = 94.3613
FEATURE [TechDraw::DrawViewDimension] Dimension029
  AngleOverride = false
  Arbitrary = false
  ArbitraryTolerances = false
  BoxCorners = (2) [(-152.257,-114.765,-1e-07),(152.257,114.765,1e-07)]
  EqualTolerance = true
  ExtensionAngle = 0
  FormatSpec = %.2w
  FormatSpecOverTolerance = %+.2w
  FormatSpecUnderTolerance = %+.2w
  Inverted = false
  LineAngle = 0
  LockPosition = false
  MeasureType = 1
  OverTolerance = 0
  References2D = -> [View001]
  Rotation = 0
  ScaleType = 0
  TheoreticalExact = false
  Type = 0
  UnderTolerance = 0
  X = -79.6886
  Y = 57.2837
FEATURE [TechDraw::DrawViewDimension] Dimension030
  AngleOverride = false
  Arbitrary = false
  ArbitraryTolerances = false
  BoxCorners = (2) [(-152.257,-114.765,-1e-07),(152.257,114.765,1e-07)]
  EqualTolerance = true
  ExtensionAngle = 0
  FormatSpec = %.2w
  FormatSpecOverTolerance = %+.2w
  FormatSpecUnderTolerance = %+.2w
  Inverted = false
  LineAngle = 0
  LockPosition = false
  MeasureType = 1
  OverTolerance = 0
  References2D = -> [View001]
  Rotation = 0
  ScaleType = 0
  TheoreticalExact = false
  Type = 6
  UnderTolerance = 0
  X = 20.2048
  Y = 54.1022
FEATURE [TechDraw::DrawViewDimension] Dimension032
  AngleOverride = false
  Arbitrary = false
  ArbitraryTolerances = false
  BoxCorners = (2) [(-152.257,-114.765,-1e-07),(152.257,114.765,1e-07)]
  EqualTolerance = true
  ExtensionAngle = 0
  FormatSpec = %.2w
  FormatSpecOverTolerance = %+.2w
  FormatSpecUnderTolerance = %+.2w
  Inverted = false
  LineAngle = 0
  LockPosition = false
  MeasureType = 1
  OverTolerance = 0
  References2D = -> [View001]
  Rotation = 0
  ScaleType = 0
  TheoreticalExact = false
  Type = 0
  UnderTolerance = 0
  X = -80.6008
  Y = -33.183
FEATURE [TechDraw::DrawViewDimension] Dimension033
  AngleOverride = false
  Arbitrary = false
  ArbitraryTolerances = false
  BoxCorners = (2) [(-152.257,-114.765,-1e-07),(152.257,114.765,1e-07)]
  EqualTolerance = true
  ExtensionAngle = 0
  FormatSpec = %.2w
  FormatSpecOverTolerance = %+.2w
  FormatSpecUnderTolerance = %+.2w
  Inverted = false
  LineAngle = 0
  LockPosition = false
  MeasureType = 1
  OverTolerance = 0
  References2D = -> [View001]
  Rotation = 0
  ScaleType = 0
  TheoreticalExact = false
  Type = 0
  UnderTolerance = 0
  X = 158.714
  Y = 69.2232
FEATURE [TechDraw::DrawPage] Page001  label="A3_drawing"
  KeepUpdated = true
  NextBalloonIndex = 1
  ProjectionType = 0
  Template = -> Template001
  Views = -> [View001,DimExtent,DimExtent001,Dimension012,Dimension013,Dimension014,Dimension015,Dimension016,Dimension017,Dimension018,Dimension019,Dimension020,Dimension021,Dimension022,Dimension023,Dimension024,Dimension025,Dimension026,Dimension027,Dimension028,Dimension029,Dimension030,Dimension032,Dimension033]
note: 5 file-system paths scrubbed to <path> (originals preserved in the JSON sidecar)
